FCSTD DOCUMENT  (FreeCAD 0.19R24276 (Git))
Label: Machine
License: All rights reserved
LicenseURL: http://en.wikipedia.org/wiki/All_rights_reserved
objects: Part::Feature×122, TechDraw::DrawViewDimension×35, Sketcher::SketchObject×31, PartDesign::Hole×19, PartDesign::Body×13, App::DocumentObjectGroup×9, App::Part×8, PartDesign::FeatureBase×7, PartDesign::Pad×6, PartDesign::Pocket×4, PartDesign::SubShapeBinder×3, TechDraw::DrawSVGTemplate×2, TechDraw::DrawViewPart×2, TechDraw::DrawViewAnnotation×2, TechDraw::DrawPage×2, Spreadsheet::Sheet×1, Mesh::Feature×1, App::VRMLObject×1, App::Link×1
note: 234 computed .brp shape members not serialized (recipe doc carries the construction recipe); baked Part::Feature solids carry a one-line shape summary decoded from their .brp

FEATURE [Sketcher::SketchObject] Sketch003
  FullyConstrained = false
  MapMode = 5
  Placement = pos=(0,0,0) rot=(1,0,0;1.5708rad)
  Support = -> [XZ_Plane002]
  expr: Constraints[11] = Spreadsheet.machine_heigh
  expr: Constraints[34] = 25 + Spreadsheet.rail_wheel_outer_clearing
  expr: Constraints[35] = 25 + Spreadsheet.rail_wheel_outer_clearing
  sketch-geometry (15):
    g0: LineSegment StartX=-20 StartY=140 StartZ=0 EndX=26 EndY=140 EndZ=0
    g1: LineSegment StartX=26 StartY=140 StartZ=0 EndX=26 EndY=0 EndZ=0
    g2: LineSegment StartX=26 StartY=0 StartZ=0 EndX=-20 EndY=0 EndZ=0
    g3: LineSegment StartX=-20 StartY=0 StartZ=0 EndX=-20 EndY=140 EndZ=0
    g4: GeomPoint X=0 Y=0 Z=0
    g5: LineSegment StartX=3.41 StartY=104.4 StartZ=0 EndX=11.59 EndY=104.4 EndZ=0
    g6: LineSegment StartX=13.5 StartY=102.49 StartZ=0 EndX=13.5 EndY=101.04 EndZ=0
    g7: LineSegment StartX=11.59 StartY=99.13 StartZ=0 EndX=3.41 EndY=99.13 EndZ=0
    g8: LineSegment StartX=1.5 StartY=101.04 StartZ=0 EndX=1.5 EndY=102.49 EndZ=0
    g9: ArcOfCircle CenterX=3.41 CenterY=102.49 CenterZ=0 NormalX=0 NormalY=0 NormalZ=1 AngleXU=0 Radius=1.91 StartAngle=1.5708 EndAngle=3.14159
    g10: ArcOfCircle CenterX=3.41 CenterY=101.04 CenterZ=0 NormalX=0 NormalY=0 NormalZ=1 AngleXU=0 Radius=1.91 StartAngle=3.14159 EndAngle=4.71239
    g11: ArcOfCircle CenterX=11.59 CenterY=102.49 CenterZ=0 NormalX=0 NormalY=0 NormalZ=1 AngleXU=0 Radius=1.91 StartAngle=1e-16 EndAngle=1.5708
    g12: ArcOfCircle CenterX=11.59 CenterY=101.04 CenterZ=0 NormalX=0 NormalY=0 NormalZ=1 AngleXU=0 Radius=1.91 StartAngle=4.71239 EndAngle=6.28319
    g13: GeomPoint X=7.5 Y=99.13 Z=0
    g14: Circle CenterX=7.5 CenterY=120 CenterZ=0 NormalX=0 NormalY=0 NormalZ=1 AngleXU=0 Radius=4.20728
  constraints (36):
    c: Coincident(g0,g1)
    c: Coincident(g1,g2)
    c: Coincident(g2,g3)
    c: Coincident(g3,g0)
    c: Horizontal(g0)
    c: Horizontal(g2)
    c: Vertical(g1)
    c: Vertical(g3)
    c: DistanceX(g2,g2) = 46
    c: Horizontal(g4,g-1)
    c: Vertical(g4,g-1)
    c: DistanceY(g1,g1) = 140
    c: Horizontal(g5)
    c: Horizontal(g7)
    c: Vertical(g6)
    c: Vertical(g8)
    c: Tangent(g5,g9) = 1.5708
    c: Tangent(g8,g9) = 1.5708
    c: Tangent(g7,g10) = 1.5708
    c: Tangent(g8,g10) = 1.5708
    c: Tangent(g5,g11) = 1.5708
    c: Tangent(g6,g11) = 1.5708
    c: Tangent(g6,g12) = 1.5708
    c: Tangent(g7,g12) = 1.5708
    c: DistanceX(g8,g6) = 12
    c: Symmetric(g7,g7,g13)
    c: Equal(g12,g11)
    c: Equal(g11,g9)
    c: Equal(g9,g10)
    c: DistanceY(g14,g0) = 20
    c: DistanceY(g5,g14) = 15.6
    c: DistanceY(g7,g5) = 5.27
    c: DistanceY(g8,g8) = 1.45
    c: Block(g3)
    c: DistanceX(g0,g14) = 27.5
    c: DistanceX(g0,g13) = 27.5
FEATURE [PartDesign::Pad] Pad001  label="Frame Plate Body"
  Direction = (1,1,1)
  Length = 8
  Length2 = 100
  Placement = pos=(0,0,0) rot=(1,0,0;1.5708rad)
  Profile = -> Sketch003
  Reversed = true
  Type = 0
FEATURE [Sketcher::SketchObject] Sketch004
  ExternalGeometry = -> [Pad001,Sketch003]
  FullyConstrained = true
  MapMode = 5
  Placement = pos=(0,0,0) rot=(1,0,0;1.5708rad)
  Support = -> [XZ_Plane002]
  expr: Constraints[19] = Spreadsheet.machine_heigh - Spreadsheet.board_heigh_from_top - 35.1
  expr: Constraints[22] = Spreadsheet.machine_heigh - Spreadsheet.bed_support_height + 20
  expr: Constraints[26] = 25 + Spreadsheet.rail_wheel_outer_clearing
  sketch-geometry (10):
    g0: Circle CenterX=-10 CenterY=10 CenterZ=0 NormalX=0 NormalY=0 NormalZ=1 AngleXU=0 Radius=2.5
    g1: Circle CenterX=10 CenterY=10 CenterZ=0 NormalX=0 NormalY=0 NormalZ=1 AngleXU=0 Radius=2.5
    g2: LineSegment StartX=-10 StartY=10 StartZ=0 EndX=10 EndY=10 EndZ=0
    g3: GeomPoint X=0 Y=10 Z=0
    g4: Circle CenterX=7.5 CenterY=130 CenterZ=0 NormalX=0 NormalY=0 NormalZ=1 AngleXU=0 Radius=2.5
    g5: Circle CenterX=7.5 CenterY=110 CenterZ=0 NormalX=0 NormalY=0 NormalZ=1 AngleXU=0 Radius=2.5
    g6: Circle CenterX=-10 CenterY=44.9 CenterZ=0 NormalX=0 NormalY=0 NormalZ=1 AngleXU=0 Radius=2.5
    g7: Circle CenterX=10 CenterY=44.9 CenterZ=0 NormalX=0 NormalY=0 NormalZ=1 AngleXU=0 Radius=2.5
    g8: Circle CenterX=-10 CenterY=60.9 CenterZ=0 NormalX=0 NormalY=0 NormalZ=1 AngleXU=0 Radius=2.5
    g9: Circle CenterX=10 CenterY=60.9 CenterZ=0 NormalX=0 NormalY=0 NormalZ=1 AngleXU=0 Radius=2.5
  constraints (27):
    c: Radius(g0) = 2.5
    c: Equal(g0,g1)
    c: Horizontal(g0,g1)
    c: DistanceX(g0,g1) = 20
    c: Coincident(g2,g0)
    c: Coincident(g2,g1)
    c: Symmetric(g2,g2,g3)
    c: Vertical(g3,g-1)
    c: DistanceY(g-1,g3) = 10
    c: Vertical(g5,g4)
    c: Equal(g5,g4)
    c: Equal(g4,g1)
    c: DistanceY(g5,g4) = 20
    c: DistanceY(g4,g-5) = 10
    c: Equal(g6,g7)
    c: Equal(g7,g0)
    c: Vertical(g6,g0)
    c: Vertical(g7,g1)
    c: Horizontal(g6,g7)
    c: DistanceY(g-4,g6) = 44.9
    c: Equal(g8,g9)
    c: Equal(g9,g6)
    c: DistanceY(g-1,g8) = 60.9
    c: Horizontal(g8,g9)
    c: Vertical(g6,g8)
    c: Vertical(g7,g9)
    c: DistanceX(g-3,g4) = 27.5
FEATURE [PartDesign::Hole] Hole  label="Frame Plate Mount Holes 1"
  BaseFeature = -> Pad001
  Depth = 25
  DepthType = 0
  Diameter = 5.5
  DrillForDepth = false
  DrillPoint = 0
  DrillPointAngle = 118
  HoleCutCountersinkAngle = 90
  HoleCutCustomValues = false
  HoleCutDepth = 5.4
  HoleCutDiameter = 9.2
  HoleCutType = 0
  ModelActualThread = false
  Placement = pos=(0,0,0) rot=(1,0,0;1.5708rad)
  Profile = -> Sketch004
  Tapered = false
  TaperedAngle = 90
  ThreadAngle = 0
  ThreadClass = 0
  ThreadCutOffInner = 0
  ThreadCutOffOuter = 0
  ThreadDirection = 0
  ThreadFit = 0
  ThreadPitch = 0
  ThreadSize = 13
  ThreadType = 1
  Threaded = false
FEATURE [PartDesign::Body] Body002  label="Front Left Plate Frame"
  Group = -> [Sketch003,Pad001,Sketch004,Hole]
  Origin = -> Origin002
  Placement = pos=(20,0,0) rot=(0,0,1;3.14159rad)
  Tip = -> Hole
  expr: .Placement.Base.x = 20
FEATURE [Part::Feature] Part__Feature001  label="Y-Axis Left Rail"
  Placement = pos=(12.5,0,120) rot=(-1,0,0;1.5708rad)
  shape: bbox 20 x 500 x 40 mm, 116 faces (baked)
  expr: .Placement.Base.z = Spreadsheet.machine_heigh - 20
  expr: .Placement.Base.x = 10 + Spreadsheet.rail_wheel_outer_clearing
FEATURE [PartDesign::FeatureBase] Clone
  BaseFeature = -> Body002
  Placement = pos=(0,0,0) rot=(0,0,1;3.14159rad)
FEATURE [PartDesign::Body] Body  label="Back Left Plate Frame"
  BaseFeature = -> Body002
  Group = -> [Clone]
  Origin = -> Origin
  Placement = pos=(20,508,0) rot=(0,0,1;0rad)
  Tip = -> Clone
  expr: .Placement.Base.x = 20
FEATURE [PartDesign::FeatureBase] Clone001
  BaseFeature = -> Body002
  Placement = pos=(0,0,0) rot=(0,0,1;3.14159rad)
FEATURE [PartDesign::Body] Body003  label="Front Right Plate Frame"
  BaseFeature = -> Body002
  Group = -> [Clone001]
  Origin = -> Origin003
  Placement = pos=(980,-8,0) rot=(0,0,1;3.14159rad)
  Tip = -> Clone001
  expr: .Placement.Base.x = Spreadsheet.machine_length - 20
FEATURE [PartDesign::FeatureBase] Clone002
  BaseFeature = -> Body002
  Placement = pos=(0,0,0) rot=(0,0,1;3.14159rad)
FEATURE [PartDesign::Body] Body004  label="Back Right Plate Frame"
  BaseFeature = -> Body002
  Group = -> [Clone002]
  Origin = -> Origin004
  Placement = pos=(980,500,0) rot=(0,0,1;3.14159rad)
  Tip = -> Clone002
  expr: .Placement.Base.x = Spreadsheet.machine_length - 20
FEATURE [Part::Feature] Part__Feature007  label="Y-Axis Right Rail"
  Placement = pos=(987.5,0,120) rot=(-1,0,0;1.5708rad)
  shape: bbox 20 x 500 x 40 mm, 116 faces (baked)
  expr: .Placement.Base.z = Spreadsheet.machine_heigh - 20
  expr: .Placement.Base.x = Spreadsheet.machine_length - 10 - Spreadsheet.rail_wheel_outer_clearing
FEATURE [Sketcher::SketchObject] Sketch005
  FullyConstrained = true
  MapMode = 5
  Support = -> [XY_Plane005]
  expr: Constraints[9] = Spreadsheet.machine_width
  expr: Constraints[10] = Spreadsheet.machine_length
  sketch-geometry (4):
    g0: LineSegment StartX=0 StartY=500 StartZ=0 EndX=1000 EndY=500 EndZ=0
    g1: LineSegment StartX=1000 StartY=500 StartZ=0 EndX=1000 EndY=180 EndZ=0
    g2: LineSegment StartX=1000 StartY=180 StartZ=0 EndX=0 EndY=180 EndZ=0
    g3: LineSegment StartX=0 StartY=180 StartZ=0 EndX=0 EndY=500 EndZ=0
  constraints (12):
    c: Coincident(g0,g1)
    c: Coincident(g1,g2)
    c: Coincident(g2,g3)
    c: Coincident(g3,g0)
    c: Horizontal(g0)
    c: Horizontal(g2)
    c: Vertical(g1)
    c: Vertical(g3)
    c: Vertical(g2,g-1)
    c: DistanceY(g-1,g0) = 500
    c: DistanceX(g0,g0) = 1000
    c: DistanceY(g3,g3) = 320
FEATURE [PartDesign::Pad] Pad
  Direction = (1,1,1)
  Length = 20
  Length2 = 100
  Profile = -> Sketch005
  Type = 0
  expr: Length = Spreadsheet.bed_thickness
FEATURE [PartDesign::Body] Body005  label="Bed"
  Group = -> [Sketch005,Pad]
  Origin = -> Origin005
  Placement = pos=(0,0,50.9) rot=(0,0,1;0rad)
  Tip = -> Pad
  expr: .Placement.Base.z = Spreadsheet.machine_heigh - Spreadsheet.bed_support_height + 10
FEATURE [Part::Feature] Part__Feature008  label="Right001"
  shape: bbox 144 x 13.2 x 66.48 mm, 79 faces (baked)
FEATURE [Part::Feature] Part__Feature009  label="Left001"
  shape: bbox 144 x 15 x 195 mm, 149 faces (baked)
FEATURE [App::Part] Boolean
  Group = -> [Part__Feature008,Part__Feature009]
  Origin = -> Origin006
  Placement = pos=(570,80,80) rot=(0,0,-1;1.5708rad)
  expr: .Placement.Base.x = Spreadsheet.machine_length / 2 + 70
  expr: .Placement.Base.z = Spreadsheet.machine_heigh - Spreadsheet.board_heigh_from_top
FEATURE [Spreadsheet::Sheet] Spreadsheet
  cells = A2=Bed Thickness; B2(bed_thickness)=20; E2=Bed Support Height; F2(bed_support_height)==board_heigh_from_top + bed_thickness + board_fix_heigh + 10; A3=Board Heigh; B3(board_heigh)=80; A4=Board Fix Height; B4(board_fix_heigh)=9.1; A5=Rail Wheel Width; B5(rail_wheel_width)=11; A6=Rail Wheel Spacers; B6(rail_wheel_spacers)=7; A7=Rail Wheel Outer Clearing; B7(rail_wheel_outer_clearing)=2.5; A8=Machine Width; B8(machine_width)=500; A9=Machine Length; B9(machine_length)=1000; A10=Power Supply Length; B10(power_supply_length)=210; A11=Machine Heigh; B11(machine_heigh)=140; A12=Board Heigh From Top; B12(board_heigh_from_top)=60; A13=Y Axis Position; B13(y_axis_pos)=283; D13=75; E13=475
FEATURE [Mesh::Feature] ed1_board_support  label="ed1-board-support"
  Placement = pos=(430,190,75.45) rot=(0,0,1;0rad)
  expr: .Placement.Base.x = Spreadsheet.machine_length / 2 - 70
  expr: .Placement.Base.z = -Spreadsheet.board_fix_heigh / 2 + Spreadsheet.machine_heigh - Spreadsheet.board_heigh_from_top
FEATURE [Sketcher::SketchObject] Sketch009
  FullyConstrained = true
  expr: Constraints[11] = Spreadsheet.machine_width
  expr: Constraints[10] = Spreadsheet.machine_length
  sketch-geometry (4):
    g0: LineSegment StartX=0 StartY=500 StartZ=0 EndX=1000 EndY=500 EndZ=0
    g1: LineSegment StartX=1000 StartY=500 StartZ=0 EndX=1000 EndY=0 EndZ=0
    g2: LineSegment StartX=1000 StartY=0 StartZ=0 EndX=0 EndY=0 EndZ=0
    g3: LineSegment StartX=0 StartY=0 StartZ=0 EndX=0 EndY=500 EndZ=0
  constraints (12):
    c: Coincident(g0,g1)
    c: Coincident(g1,g2)
    c: Coincident(g2,g3)
    c: Coincident(g3,g0)
    c: Horizontal(g0)
    c: Horizontal(g2)
    c: Vertical(g1)
    c: Vertical(g3)
    c: Vertical(g2,g-1)
    c: Horizontal(g2,g-1)
    c: DistanceX(g0,g0) = 1000
    c: DistanceY(g3,g3) = 500
FEATURE [App::DocumentObjectGroup] Group004  label="Feeder"
  Group = -> [Boolean]
FEATURE [Part::Feature] Part__Feature106  label="Bottom Camera"
  Placement = pos=(500,102.5,40.9) rot=(1,0,0;1.5708rad)
  shape: bbox 38.04 x 38.04 x 27.94 mm, 666 faces, 0 solids (baked)
  expr: .Placement.Base.z = Spreadsheet.board_heigh - Spreadsheet.board_fix_heigh - 30
  expr: .Placement.Base.x = Spreadsheet.machine_length / 2
FEATURE [Part::Feature] Part__Feature107  label="V-Slot 20x40x1000 Linear Rail"
  Placement = pos=(0,306.5,165) rot=(0.57735,0.57735,0.57735;2.0944rad)
  shape: bbox 1000 x 20 x 40 mm, 116 faces (baked)
  expr: .Placement.Base.y = Spreadsheet.y_axis_pos + 23.5
  expr: .Placement.Base.z = Spreadsheet.machine_heigh + 25
  expr: .Placement.Base.x = 0
FEATURE [App::VRMLObject] OpenPNPControl
  Placement = pos=(955,508,25) rot=(0,0,-1;1.5708rad)
FEATURE [Part::Feature] Part__Feature120  label="Bottom Right Frame"
  Placement = pos=(980,0,10) rot=(0.57735,-0.57735,-0.57735;4.18879rad)
  shape: bbox 40 x 500 x 20 mm, 116 faces (baked)
  expr: .Placement.Base.x = Spreadsheet.machine_length - 20
  expr: .Placement.Base.z = 10
FEATURE [Part::Feature] Part__Feature121  label="Bottom Left Frame"
  Placement = pos=(20,0,10) rot=(0.57735,-0.57735,-0.57735;4.18879rad)
  shape: bbox 40 x 500 x 20 mm, 116 faces (baked)
  expr: .Placement.Base.x = 20
FEATURE [Part::Feature] Part__Feature014  label="SWP (Basis)"
  Placement = pos=(-2.4e-14,1.75,57) rot=(-1,0,0;1.5708rad)
  shape: bbox 215 x 51.27 x 114 mm, 686 faces (baked)
FEATURE [Part::Feature] Part__Feature015  label="SWP (Deksel)"
  Placement = pos=(-18.25,51.25,57) rot=(-1,0,0;1.5708rad)
  shape: bbox 195 x 25.77 x 110.5 mm, 202 faces (baked)
FEATURE [Part::Feature] Part__Feature016  label="Slotted Countersunk Flat Head Screw_DIN_ISO 2009 - M3 x 5 --- 5N"
  Placement = pos=(-154,44.75,114) rot=(0.706406,-0.044508,-0.706406;3.23055rad)
  shape: bbox 5.5 x 5.5 x 5 mm, 14 faces (baked)
FEATURE [Part::Feature] Part__Feature017  label="Slotted Countersunk Flat Head Screw_DIN_ISO 2009 - M3 x 5 --- 5N001"
  Placement = pos=(-33,44.75,114) rot=(-0.51498,0.685268,0.51498;1.94005rad)
  shape: bbox 5.5 x 5.5 x 5 mm, 14 faces (baked)
FEATURE [Part::Feature] Part__Feature018  label="Slotted Countersunk Flat Head Screw_DIN_ISO 2009 - M3 x 5 --- 5N002"
  Placement = pos=(-154,44.75,6.765e-12) rot=(0.57735,0.57735,0.57735;4.18879rad)
  shape: bbox 5.5 x 5.5 x 5 mm, 14 faces (baked)
FEATURE [Part::Feature] Part__Feature019  label="Slotted Countersunk Flat Head Screw_DIN_ISO 2009 - M3 x 5 --- 5N003"
  Placement = pos=(-33,44.75,6.772e-12) rot=(0.24005,-0.940613,0.24005;1.63198rad)
  shape: bbox 5.5 x 5.5 x 5 mm, 14 faces (baked)
FEATURE [Part::Feature] Part__Feature020  label="Slotted Countersunk Flat Head Screw_DIN_ISO 2009 - M3 x 5 --- 5N004"
  Placement = pos=(-215,44.75,102) rot=(-1,0,0;2.08794rad)
  shape: bbox 5 x 5.5 x 5.5 mm, 14 faces (baked)
FEATURE [Part::Feature] Part__Feature021  label="Slotted Countersunk Flat Head Screw_DIN_ISO 2009 - M3 x 5 --- 5N005"
  Placement = pos=(-215,44.75,12) rot=(-1,0,0;0.866489rad)
  shape: bbox 5 x 5.5 x 5.5 mm, 14 faces (baked)
FEATURE [Part::Feature] Part__Feature022  label="Body 60mm fan"
  Placement = pos=(-170.75,34.3,77.75) rot=(-1,0,0;1.5708rad)
  shape: bbox 59.5 x 15.2 x 59.5 mm, 105 faces (baked)
FEATURE [Part::Feature] Part__Feature023  label="Propellor 60mm fan"
  Placement = pos=(-170.75,44.3,77.75) rot=(-0.793222,0.430581,0.430581;1.8004rad)
  shape: bbox 57.7 x 10.4 x 57.19 mm, 97 faces (baked)
FEATURE [Part::Feature] Part__Feature024  label="Slotted Countersunk Flat Head Screw_DIN_ISO 2009 - M3 x 20 --- 20N"
  Placement = pos=(-145.75,51.25,52.75) rot=(0.700883,-0.700883,0.13239;3.40484rad)
  shape: bbox 5.5 x 20 x 5.5 mm, 14 faces (baked)
FEATURE [Part::Feature] Part__Feature025  label="Slotted Countersunk Flat Head Screw_DIN_ISO 2009 - M3 x 20 --- 20N001"
  Placement = pos=(-195.75,51.25,102.75) rot=(0.672053,-0.672053,0.310951;3.74454rad)
  shape: bbox 5.5 x 20 x 5.5 mm, 14 faces (baked)
FEATURE [Part::Feature] Part__Feature026  label="SWP (M3 moer)"
  Placement = pos=(-205,-1.3e-14,104.5) rot=(-1,0,0;1.5708rad)
  shape: bbox 8.083 x 3.75 x 7 mm, 29 faces (baked)
FEATURE [Part::Feature] Part__Feature027  label="SWP (M3 moer)001"
  Placement = pos=(-205,0,9.5) rot=(-1,0,0;1.5708rad)
  shape: bbox 8.083 x 3.75 x 7 mm, 29 faces (baked)
FEATURE [Part::Feature] Part__Feature028  label="SWP (M3 moer)002"
  Placement = pos=(-117.5,-7e-15,50.05) rot=(-1,0,0;1.5708rad)
  shape: bbox 8.083 x 3.75 x 7 mm, 29 faces (baked)
FEATURE [Part::Feature] Part__Feature029  label="SWP (M3 moer)003"
  Placement = pos=(-27.5,-1.3e-14,104.5) rot=(-1,0,0;1.5708rad)
  shape: bbox 8.083 x 3.75 x 7 mm, 29 faces (baked)
FEATURE [Part::Feature] Part__Feature030  label="SWP (M3 moer)004"
  Placement = pos=(-27.5,-1e-15,9.5) rot=(-1,0,0;1.5708rad)
  shape: bbox 8.083 x 3.75 x 7 mm, 29 faces (baked)
FEATURE [Part::Feature] Part__Feature031  label="SWP (PCB)"
  Placement = pos=(-1.75,9.75,57) rot=(-1,0,0;1.5708rad)
  shape: bbox 211.5 x 15.9 x 110.5 mm, 247 faces (baked)
FEATURE [Part::Feature] Part__Feature032  label="SWP (Montage draad)"
  Placement = pos=(-9.8,18.4,88.95) rot=(0.57735,0.57735,0.57735;4.18879rad)
  shape: bbox 9.9 x 4.25 x 7 mm, 32 faces (baked)
FEATURE [Part::Feature] Part__Feature033  label="SWP (Montage draad 2)"
  Placement = pos=(-9.8,18.4,88.95) rot=(-1,0,0;1.5708rad)
  shape: bbox 7 x 1 x 7 mm, 27 faces (baked)
FEATURE [Part::Feature] Part__Feature034  label="Slotted Cheese Head Screw_DIN_ISO 1207 - M4 x 5 --- 5N"
  Placement = pos=(-9.8,22,88.95) rot=(-0.497229,0.497229,-0.711004;1.90545rad)
  shape: bbox 7.022 x 7.6 x 7 mm, 13 faces (baked)
FEATURE [Part::Feature] Part__Feature035  label="SWP (Montage draad)001"
  Placement = pos=(-9.8,18.4,79.45) rot=(0.57735,0.57735,0.57735;4.18879rad)
  shape: bbox 9.9 x 4.25 x 7 mm, 32 faces (baked)
FEATURE [Part::Feature] Part__Feature036  label="SWP (Montage draad)002"
  Placement = pos=(-9.8,18.4,69.95) rot=(0.57735,0.57735,0.57735;4.18879rad)
  shape: bbox 9.9 x 4.25 x 7 mm, 32 faces (baked)
FEATURE [Part::Feature] Part__Feature037  label="SWP (Montage draad)003"
  Placement = pos=(-9.8,18.4,60.45) rot=(0.57735,0.57735,0.57735;4.18879rad)
  shape: bbox 9.9 x 4.25 x 7 mm, 32 faces (baked)
FEATURE [Part::Feature] Part__Feature038  label="SWP (Montage draad)004"
  Placement = pos=(-9.8,18.4,50.95) rot=(0.57735,0.57735,0.57735;4.18879rad)
  shape: bbox 9.9 x 4.25 x 7 mm, 32 faces (baked)
FEATURE [Part::Feature] Part__Feature039  label="SWP (Montage draad)005"
  Placement = pos=(-9.8,18.4,41.45) rot=(0.57735,0.57735,0.57735;4.18879rad)
  shape: bbox 9.9 x 4.25 x 7 mm, 32 faces (baked)
FEATURE [Part::Feature] Part__Feature040  label="SWP (Montage draad)006"
  Placement = pos=(-9.8,18.4,31.95) rot=(0.57735,0.57735,0.57735;4.18879rad)
  shape: bbox 9.9 x 4.25 x 7 mm, 32 faces (baked)
FEATURE [Part::Feature] Part__Feature041  label="SWP (Montage draad)007"
  Placement = pos=(-9.8,18.4,22.45) rot=(0.57735,0.57735,0.57735;4.18879rad)
  shape: bbox 9.9 x 4.25 x 7 mm, 32 faces (baked)
FEATURE [Part::Feature] Part__Feature042  label="SWP (Montage draad)008"
  Placement = pos=(-9.8,18.4,12.95) rot=(0.57735,0.57735,0.57735;4.18879rad)
  shape: bbox 9.9 x 4.25 x 7 mm, 32 faces (baked)
FEATURE [Part::Feature] Part__Feature043  label="SWP (Montage draad 2)001"
  Placement = pos=(-9.8,18.4,79.45) rot=(-1,0,0;1.5708rad)
  shape: bbox 7 x 1 x 7 mm, 27 faces (baked)
FEATURE [Part::Feature] Part__Feature044  label="SWP (Montage draad 2)002"
  Placement = pos=(-9.8,18.4,69.95) rot=(-1,0,0;1.5708rad)
  shape: bbox 7 x 1 x 7 mm, 27 faces (baked)
FEATURE [Part::Feature] Part__Feature045  label="SWP (Montage draad 2)003"
  Placement = pos=(-9.8,18.4,60.45) rot=(-1,0,0;1.5708rad)
  shape: bbox 7 x 1 x 7 mm, 27 faces (baked)
FEATURE [Part::Feature] Part__Feature046  label="SWP (Montage draad 2)004"
  Placement = pos=(-9.8,18.4,50.95) rot=(-1,0,0;1.5708rad)
  shape: bbox 7 x 1 x 7 mm, 27 faces (baked)
FEATURE [Part::Feature] Part__Feature047  label="SWP (Montage draad 2)005"
  Placement = pos=(-9.8,18.4,41.45) rot=(-1,0,0;1.5708rad)
  shape: bbox 7 x 1 x 7 mm, 27 faces (baked)
FEATURE [Part::Feature] Part__Feature048  label="SWP (Montage draad 2)006"
  Placement = pos=(-9.8,18.4,31.95) rot=(-1,0,0;1.5708rad)
  shape: bbox 7 x 1 x 7 mm, 27 faces (baked)
FEATURE [Part::Feature] Part__Feature049  label="SWP (Montage draad 2)007"
  Placement = pos=(-9.8,18.4,22.45) rot=(-1,0,0;1.5708rad)
  shape: bbox 7 x 1 x 7 mm, 27 faces (baked)
FEATURE [Part::Feature] Part__Feature050  label="SWP (Montage draad 2)008"
  Placement = pos=(-9.8,18.4,12.95) rot=(-1,0,0;1.5708rad)
  shape: bbox 7 x 1 x 7 mm, 27 faces (baked)
FEATURE [Part::Feature] Part__Feature051  label="Slotted Cheese Head Screw_DIN_ISO 1207 - M4 x 5 --- 5N001"
  Placement = pos=(-9.8,22,79.45) rot=(-0.497229,0.497229,-0.711004;1.90545rad)
  shape: bbox 7.022 x 7.6 x 7 mm, 13 faces (baked)
FEATURE [Part::Feature] Part__Feature052  label="Slotted Cheese Head Screw_DIN_ISO 1207 - M4 x 5 --- 5N002"
  Placement = pos=(-9.8,22,69.95) rot=(-0.497229,0.497229,-0.711004;1.90545rad)
  shape: bbox 7.022 x 7.6 x 7 mm, 13 faces (baked)
FEATURE [Part::Feature] Part__Feature053  label="Slotted Cheese Head Screw_DIN_ISO 1207 - M4 x 5 --- 5N003"
  Placement = pos=(-9.8,22,60.45) rot=(-0.497229,0.497229,-0.711004;1.90545rad)
  shape: bbox 7.022 x 7.6 x 7 mm, 13 faces (baked)
FEATURE [Part::Feature] Part__Feature054  label="Slotted Cheese Head Screw_DIN_ISO 1207 - M4 x 5 --- 5N004"
  Placement = pos=(-9.8,22,50.95) rot=(-0.497229,0.497229,-0.711004;1.90545rad)
  shape: bbox 7.022 x 7.6 x 7 mm, 13 faces (baked)
FEATURE [Part::Feature] Part__Feature055  label="Slotted Cheese Head Screw_DIN_ISO 1207 - M4 x 5 --- 5N005"
  Placement = pos=(-9.8,22,41.45) rot=(-0.497229,0.497229,-0.711004;1.90545rad)
  shape: bbox 7.022 x 7.6 x 7 mm, 13 faces (baked)
FEATURE [Part::Feature] Part__Feature056  label="Slotted Cheese Head Screw_DIN_ISO 1207 - M4 x 5 --- 5N006"
  Placement = pos=(-9.8,22,31.95) rot=(-0.497229,0.497229,-0.711004;1.90545rad)
  shape: bbox 7.022 x 7.6 x 7 mm, 13 faces (baked)
FEATURE [Part::Feature] Part__Feature057  label="Slotted Cheese Head Screw_DIN_ISO 1207 - M4 x 5 --- 5N007"
  Placement = pos=(-9.8,22,22.45) rot=(-0.497229,0.497229,-0.711004;1.90545rad)
  shape: bbox 7.022 x 7.6 x 7 mm, 13 faces (baked)
FEATURE [Part::Feature] Part__Feature058  label="Slotted Cheese Head Screw_DIN_ISO 1207 - M4 x 5 --- 5N008"
  Placement = pos=(-9.8,22,12.95) rot=(-0.497229,0.497229,-0.711004;1.90545rad)
  shape: bbox 7.022 x 7.6 x 7 mm, 13 faces (baked)
FEATURE [Part::Feature] Part__Feature059  label="SWP (switch)"
  Placement = pos=(-128.5,14.3,-4.2e-14) rot=(0,1,0;3.14159rad)
  shape: bbox 19 x 12.1 x 6 mm, 97 faces (baked)
FEATURE [App::Part] Switching_power_supply  label="24 V power supply"
  Group = -> [Part__Feature014,Part__Feature015,Part__Feature016,Part__Feature017,Part__Feature018,Part__Feature019,Part__Feature020,Part__Feature021,Part__Feature022,Part__Feature023,Part__Feature024,Part__Feature025,Part__Feature026,Part__Feature027,Part__Feature028,Part__Feature029,Part__Feature030,Part__Feature031,Part__Feature032,Part__Feature033,Part__Feature034,Part__Feature035,Part__Feature036,+23 more]
  Origin = -> Origin009
  Placement = pos=(576,346,20) rot=(0,0.707107,0.707107;3.14159rad)
FEATURE [Part::Feature] Part__Feature060  label="SWP (Basis)001"
  Placement = pos=(-2.4e-14,1.75,57) rot=(-1,0,0;1.5708rad)
  shape: bbox 215 x 51.27 x 114 mm, 686 faces (baked)
FEATURE [Part::Feature] Part__Feature061  label="SWP (Deksel)001"
  Placement = pos=(-18.25,51.25,57) rot=(-1,0,0;1.5708rad)
  shape: bbox 195 x 25.77 x 110.5 mm, 202 faces (baked)
FEATURE [Part::Feature] Part__Feature062  label="Slotted Countersunk Flat Head Screw_DIN_ISO 2009 - M3 x 5 --- 5N006"
  Placement = pos=(-154,44.75,114) rot=(0.706406,-0.044508,-0.706406;3.23055rad)
  shape: bbox 5.5 x 5.5 x 5 mm, 14 faces (baked)
FEATURE [Part::Feature] Part__Feature063  label="Slotted Countersunk Flat Head Screw_DIN_ISO 2009 - M3 x 5 --- 5N007"
  Placement = pos=(-33,44.75,114) rot=(-0.51498,0.685268,0.51498;1.94005rad)
  shape: bbox 5.5 x 5.5 x 5 mm, 14 faces (baked)
FEATURE [Part::Feature] Part__Feature064  label="Slotted Countersunk Flat Head Screw_DIN_ISO 2009 - M3 x 5 --- 5N008"
  Placement = pos=(-154,44.75,6.765e-12) rot=(0.57735,0.57735,0.57735;4.18879rad)
  shape: bbox 5.5 x 5.5 x 5 mm, 14 faces (baked)
FEATURE [Part::Feature] Part__Feature065  label="Slotted Countersunk Flat Head Screw_DIN_ISO 2009 - M3 x 5 --- 5N009"
  Placement = pos=(-33,44.75,6.772e-12) rot=(0.24005,-0.940613,0.24005;1.63198rad)
  shape: bbox 5.5 x 5.5 x 5 mm, 14 faces (baked)
FEATURE [Part::Feature] Part__Feature066  label="Slotted Countersunk Flat Head Screw_DIN_ISO 2009 - M3 x 5 --- 5N010"
  Placement = pos=(-215,44.75,102) rot=(-1,0,0;2.08794rad)
  shape: bbox 5 x 5.5 x 5.5 mm, 14 faces (baked)
FEATURE [Part::Feature] Part__Feature067  label="Slotted Countersunk Flat Head Screw_DIN_ISO 2009 - M3 x 5 --- 5N011"
  Placement = pos=(-215,44.75,12) rot=(-1,0,0;0.866489rad)
  shape: bbox 5 x 5.5 x 5.5 mm, 14 faces (baked)
FEATURE [Part::Feature] Part__Feature068  label="Body 60mm fan001"
  Placement = pos=(-170.75,34.3,77.75) rot=(-1,0,0;1.5708rad)
  shape: bbox 59.5 x 15.2 x 59.5 mm, 105 faces (baked)
FEATURE [Part::Feature] Part__Feature069  label="Propellor 60mm fan001"
  Placement = pos=(-170.75,44.3,77.75) rot=(-0.793222,0.430581,0.430581;1.8004rad)
  shape: bbox 57.7 x 10.4 x 57.19 mm, 97 faces (baked)
FEATURE [Part::Feature] Part__Feature070  label="Slotted Countersunk Flat Head Screw_DIN_ISO 2009 - M3 x 20 --- 20N002"
  Placement = pos=(-145.75,51.25,52.75) rot=(0.700883,-0.700883,0.13239;3.40484rad)
  shape: bbox 5.5 x 20 x 5.5 mm, 14 faces (baked)
FEATURE [Part::Feature] Part__Feature071  label="Slotted Countersunk Flat Head Screw_DIN_ISO 2009 - M3 x 20 --- 20N003"
  Placement = pos=(-195.75,51.25,102.75) rot=(0.672053,-0.672053,0.310951;3.74454rad)
  shape: bbox 5.5 x 20 x 5.5 mm, 14 faces (baked)
FEATURE [Part::Feature] Part__Feature072  label="SWP (M3 moer)005"
  Placement = pos=(-205,-1.3e-14,104.5) rot=(-1,0,0;1.5708rad)
  shape: bbox 8.083 x 3.75 x 7 mm, 29 faces (baked)
FEATURE [Part::Feature] Part__Feature073  label="SWP (M3 moer)006"
  Placement = pos=(-205,0,9.5) rot=(-1,0,0;1.5708rad)
  shape: bbox 8.083 x 3.75 x 7 mm, 29 faces (baked)
FEATURE [Part::Feature] Part__Feature074  label="SWP (M3 moer)007"
  Placement = pos=(-117.5,-7e-15,50.05) rot=(-1,0,0;1.5708rad)
  shape: bbox 8.083 x 3.75 x 7 mm, 29 faces (baked)
FEATURE [Part::Feature] Part__Feature075  label="SWP (M3 moer)008"
  Placement = pos=(-27.5,-1.3e-14,104.5) rot=(-1,0,0;1.5708rad)
  shape: bbox 8.083 x 3.75 x 7 mm, 29 faces (baked)
FEATURE [Part::Feature] Part__Feature076  label="SWP (M3 moer)009"
  Placement = pos=(-27.5,-1e-15,9.5) rot=(-1,0,0;1.5708rad)
  shape: bbox 8.083 x 3.75 x 7 mm, 29 faces (baked)
FEATURE [Part::Feature] Part__Feature077  label="SWP (PCB)001"
  Placement = pos=(-1.75,9.75,57) rot=(-1,0,0;1.5708rad)
  shape: bbox 211.5 x 15.9 x 110.5 mm, 247 faces (baked)
FEATURE [Part::Feature] Part__Feature078  label="SWP (Montage draad)009"
  Placement = pos=(-9.8,18.4,88.95) rot=(0.57735,0.57735,0.57735;4.18879rad)
  shape: bbox 9.9 x 4.25 x 7 mm, 32 faces (baked)
FEATURE [Part::Feature] Part__Feature079  label="SWP (Montage draad 2)009"
  Placement = pos=(-9.8,18.4,88.95) rot=(-1,0,0;1.5708rad)
  shape: bbox 7 x 1 x 7 mm, 27 faces (baked)
FEATURE [Part::Feature] Part__Feature080  label="Slotted Cheese Head Screw_DIN_ISO 1207 - M4 x 5 --- 5N009"
  Placement = pos=(-9.8,22,88.95) rot=(-0.497229,0.497229,-0.711004;1.90545rad)
  shape: bbox 7.022 x 7.6 x 7 mm, 13 faces (baked)
FEATURE [Part::Feature] Part__Feature081  label="SWP (Montage draad)010"
  Placement = pos=(-9.8,18.4,79.45) rot=(0.57735,0.57735,0.57735;4.18879rad)
  shape: bbox 9.9 x 4.25 x 7 mm, 32 faces (baked)
FEATURE [Part::Feature] Part__Feature082  label="SWP (Montage draad)011"
  Placement = pos=(-9.8,18.4,69.95) rot=(0.57735,0.57735,0.57735;4.18879rad)
  shape: bbox 9.9 x 4.25 x 7 mm, 32 faces (baked)
FEATURE [Part::Feature] Part__Feature083  label="SWP (Montage draad)012"
  Placement = pos=(-9.8,18.4,60.45) rot=(0.57735,0.57735,0.57735;4.18879rad)
  shape: bbox 9.9 x 4.25 x 7 mm, 32 faces (baked)
FEATURE [Part::Feature] Part__Feature084  label="SWP (Montage draad)013"
  Placement = pos=(-9.8,18.4,50.95) rot=(0.57735,0.57735,0.57735;4.18879rad)
  shape: bbox 9.9 x 4.25 x 7 mm, 32 faces (baked)
FEATURE [Part::Feature] Part__Feature085  label="SWP (Montage draad)014"
  Placement = pos=(-9.8,18.4,41.45) rot=(0.57735,0.57735,0.57735;4.18879rad)
  shape: bbox 9.9 x 4.25 x 7 mm, 32 faces (baked)
FEATURE [Part::Feature] Part__Feature086  label="SWP (Montage draad)015"
  Placement = pos=(-9.8,18.4,31.95) rot=(0.57735,0.57735,0.57735;4.18879rad)
  shape: bbox 9.9 x 4.25 x 7 mm, 32 faces (baked)
FEATURE [Part::Feature] Part__Feature087  label="SWP (Montage draad)016"
  Placement = pos=(-9.8,18.4,22.45) rot=(0.57735,0.57735,0.57735;4.18879rad)
  shape: bbox 9.9 x 4.25 x 7 mm, 32 faces (baked)
FEATURE [Part::Feature] Part__Feature088  label="SWP (Montage draad)017"
  Placement = pos=(-9.8,18.4,12.95) rot=(0.57735,0.57735,0.57735;4.18879rad)
  shape: bbox 9.9 x 4.25 x 7 mm, 32 faces (baked)
FEATURE [Part::Feature] Part__Feature089  label="SWP (Montage draad 2)010"
  Placement = pos=(-9.8,18.4,79.45) rot=(-1,0,0;1.5708rad)
  shape: bbox 7 x 1 x 7 mm, 27 faces (baked)
FEATURE [Part::Feature] Part__Feature090  label="SWP (Montage draad 2)011"
  Placement = pos=(-9.8,18.4,69.95) rot=(-1,0,0;1.5708rad)
  shape: bbox 7 x 1 x 7 mm, 27 faces (baked)
FEATURE [Part::Feature] Part__Feature091  label="SWP (Montage draad 2)012"
  Placement = pos=(-9.8,18.4,60.45) rot=(-1,0,0;1.5708rad)
  shape: bbox 7 x 1 x 7 mm, 27 faces (baked)
FEATURE [Part::Feature] Part__Feature092  label="SWP (Montage draad 2)013"
  Placement = pos=(-9.8,18.4,50.95) rot=(-1,0,0;1.5708rad)
  shape: bbox 7 x 1 x 7 mm, 27 faces (baked)
FEATURE [Part::Feature] Part__Feature093  label="SWP (Montage draad 2)014"
  Placement = pos=(-9.8,18.4,41.45) rot=(-1,0,0;1.5708rad)
  shape: bbox 7 x 1 x 7 mm, 27 faces (baked)
FEATURE [Part::Feature] Part__Feature094  label="SWP (Montage draad 2)015"
  Placement = pos=(-9.8,18.4,31.95) rot=(-1,0,0;1.5708rad)
  shape: bbox 7 x 1 x 7 mm, 27 faces (baked)
FEATURE [Part::Feature] Part__Feature095  label="SWP (Montage draad 2)016"
  Placement = pos=(-9.8,18.4,22.45) rot=(-1,0,0;1.5708rad)
  shape: bbox 7 x 1 x 7 mm, 27 faces (baked)
FEATURE [Part::Feature] Part__Feature096  label="SWP (Montage draad 2)017"
  Placement = pos=(-9.8,18.4,12.95) rot=(-1,0,0;1.5708rad)
  shape: bbox 7 x 1 x 7 mm, 27 faces (baked)
FEATURE [Part::Feature] Part__Feature097  label="Slotted Cheese Head Screw_DIN_ISO 1207 - M4 x 5 --- 5N010"
  Placement = pos=(-9.8,22,79.45) rot=(-0.497229,0.497229,-0.711004;1.90545rad)
  shape: bbox 7.022 x 7.6 x 7 mm, 13 faces (baked)
FEATURE [Part::Feature] Part__Feature098  label="Slotted Cheese Head Screw_DIN_ISO 1207 - M4 x 5 --- 5N011"
  Placement = pos=(-9.8,22,69.95) rot=(-0.497229,0.497229,-0.711004;1.90545rad)
  shape: bbox 7.022 x 7.6 x 7 mm, 13 faces (baked)
FEATURE [Part::Feature] Part__Feature099  label="Slotted Cheese Head Screw_DIN_ISO 1207 - M4 x 5 --- 5N012"
  Placement = pos=(-9.8,22,60.45) rot=(-0.497229,0.497229,-0.711004;1.90545rad)
  shape: bbox 7.022 x 7.6 x 7 mm, 13 faces (baked)
FEATURE [Part::Feature] Part__Feature100  label="Slotted Cheese Head Screw_DIN_ISO 1207 - M4 x 5 --- 5N013"
  Placement = pos=(-9.8,22,50.95) rot=(-0.497229,0.497229,-0.711004;1.90545rad)
  shape: bbox 7.022 x 7.6 x 7 mm, 13 faces (baked)
FEATURE [Part::Feature] Part__Feature101  label="Slotted Cheese Head Screw_DIN_ISO 1207 - M4 x 5 --- 5N014"
  Placement = pos=(-9.8,22,41.45) rot=(-0.497229,0.497229,-0.711004;1.90545rad)
  shape: bbox 7.022 x 7.6 x 7 mm, 13 faces (baked)
FEATURE [Part::Feature] Part__Feature102  label="Slotted Cheese Head Screw_DIN_ISO 1207 - M4 x 5 --- 5N015"
  Placement = pos=(-9.8,22,31.95) rot=(-0.497229,0.497229,-0.711004;1.90545rad)
  shape: bbox 7.022 x 7.6 x 7 mm, 13 faces (baked)
FEATURE [Part::Feature] Part__Feature103  label="Slotted Cheese Head Screw_DIN_ISO 1207 - M4 x 5 --- 5N016"
  Placement = pos=(-9.8,22,22.45) rot=(-0.497229,0.497229,-0.711004;1.90545rad)
  shape: bbox 7.022 x 7.6 x 7 mm, 13 faces (baked)
FEATURE [Part::Feature] Part__Feature104  label="Slotted Cheese Head Screw_DIN_ISO 1207 - M4 x 5 --- 5N017"
  Placement = pos=(-9.8,22,12.95) rot=(-0.497229,0.497229,-0.711004;1.90545rad)
  shape: bbox 7.022 x 7.6 x 7 mm, 13 faces (baked)
FEATURE [Part::Feature] Part__Feature105  label="SWP (switch)001"
  Placement = pos=(-128.5,14.3,-4.2e-14) rot=(0,1,0;3.14159rad)
  shape: bbox 19 x 12.1 x 6 mm, 97 faces (baked)
FEATURE [App::Part] Switching_power_supply001  label="12 V power supply"
  Group = -> [Part__Feature060,Part__Feature061,Part__Feature062,Part__Feature063,Part__Feature064,Part__Feature065,Part__Feature066,Part__Feature067,Part__Feature068,Part__Feature069,Part__Feature070,Part__Feature071,Part__Feature072,Part__Feature073,Part__Feature074,Part__Feature075,Part__Feature076,Part__Feature077,Part__Feature078,Part__Feature079,Part__Feature080,Part__Feature081,Part__Feature082,+23 more]
  Origin = -> Origin010
  Placement = pos=(576,222,20) rot=(0,0.707107,0.707107;3.14159rad)
FEATURE [App::DocumentObjectGroup] Group005  label="Electronics"
  Group = -> [Switching_power_supply001,Switching_power_supply,Part__Feature106,OpenPNPControl]
FEATURE [Part::Feature] Feeder_8mm_Frame_fix001001001
  Placement = pos=(572.59,75,78.99) rot=(0,0,-1;1.5708rad)
  shape: bbox 84.4 x 9.9 x 20 mm, 453 faces, 0 solids (baked)
  expr: .Placement.Base.x = -69.45 + 84.40000000000001 + Spreadsheet.machine_length / 2 + 70 - 6.16 - 6.2
  expr: .Placement.Base.z = 44.74 - 20 + Spreadsheet.machine_heigh - Spreadsheet.board_heigh_from_top - 25.1 - 0.65
FEATURE [Part::Feature] Part__Feature123  label="Feeder Support Back"
  Placement = pos=(0,70,44.9) rot=(0,1,0;1.5708rad)
  shape: bbox 1000 x 20 x 20 mm, 72 faces (baked)
  expr: .Placement.Base.z = Spreadsheet.machine_heigh - Spreadsheet.board_heigh_from_top - 35.1
FEATURE [Part::Feature] Part__Feature124  label="Feeder Support Front"
  Placement = pos=(0,10,44.9) rot=(0,1,0;1.5708rad)
  shape: bbox 1000 x 20 x 20 mm, 72 faces (baked)
  expr: .Placement.Base.z = Spreadsheet.machine_heigh - Spreadsheet.board_heigh_from_top - 35.1
FEATURE [App::DocumentObjectGroup] Group003  label="Crossbar"
  Group = -> [Part__Feature123,Part__Feature124]
FEATURE [Sketcher::SketchObject] Sketch015
  FullyConstrained = true
  MapMode = 5
  Placement = pos=(0,0,0) rot=(0.57735,0.57735,0.57735;2.0944rad)
  Support = -> [YZ_Plane013]
  expr: Constraints[20] = Spreadsheet.machine_heigh - Spreadsheet.bed_support_height + 30
  expr: Constraints[7] = Spreadsheet.machine_width
  sketch-geometry (7):
    g0: LineSegment StartX=500 StartY=70.9 StartZ=0 EndX=500 EndY=0 EndZ=0
    g1: LineSegment StartX=500 StartY=0 StartZ=0 EndX=0 EndY=0 EndZ=0
    g2: LineSegment StartX=0 StartY=0 StartZ=0 EndX=0 EndY=54.9 EndZ=0
    g3: LineSegment StartX=0 StartY=54.9 StartZ=0 EndX=175 EndY=54.9 EndZ=0
    g4: LineSegment StartX=180 StartY=59.9 StartZ=0 EndX=180 EndY=70.9 EndZ=0
    g5: LineSegment StartX=180 StartY=70.9 StartZ=0 EndX=500 EndY=70.9 EndZ=0
    g6: ArcOfCircle CenterX=175 CenterY=59.9 CenterZ=0 NormalX=0 NormalY=0 NormalZ=1 AngleXU=0 Radius=5 StartAngle=4.71239 EndAngle=6.28319
  constraints (24):
    c: Coincident(g0,g1)
    c: Coincident(g1,g2)
    c: Horizontal(g1)
    c: Vertical(g0)
    c: Vertical(g2)
    c: Horizontal(g1,g-1)
    c: Vertical(g1,g-1)
    c: DistanceX(g1,g1) = 500
    c: Horizontal(g3)
    c: Vertical(g3,g2)
    c: Block(g2)
    c: Horizontal(g3,g2)
    c: Vertical(g4)
    c: Horizontal(g5)
    c: Horizontal(g5,g4)
    c: Vertical(g5,g4)
    c: Vertical(g0,g5)
    c: DistanceX(g5,g5) = 320
    c: Block(g5)
    c: Horizontal(g0,g5)
    c: DistanceY(g0,g0) = 70.9
    c: Tangent(g3,g6) = -1.5708
    c: Tangent(g4,g6) = -1.5708
    c: Radius(g6) = 5
FEATURE [PartDesign::Pad] Pad004
  Direction = (1,1,1)
  Length = 6
  Length2 = 100
  Placement = pos=(0,0,0) rot=(0.57735,0.57735,0.57735;2.0944rad)
  Profile = -> Sketch015
  Reversed = true
  Type = 0
FEATURE [Sketcher::SketchObject] Sketch016
  ExternalGeometry = -> [Sketch015]
  FullyConstrained = false
  MapMode = 5
  Placement = pos=(0,0,0) rot=(0.57735,0.57735,0.57735;2.0944rad)
  Support = -> [YZ_Plane013]
  expr: Constraints[13] = Spreadsheet.machine_heigh - Spreadsheet.bed_support_height + 20
  expr: Constraints[10] = Spreadsheet.machine_heigh - Spreadsheet.board_heigh_from_top - 35.1
  sketch-geometry (42):
    g0: Circle CenterX=10 CenterY=44.9 CenterZ=0 NormalX=0 NormalY=0 NormalZ=1 AngleXU=0 Radius=2.5
    g1: Circle CenterX=10 CenterY=10 CenterZ=0 NormalX=0 NormalY=0 NormalZ=1 AngleXU=0 Radius=2.5
    g2: Circle CenterX=70 CenterY=44.9 CenterZ=0 NormalX=0 NormalY=0 NormalZ=1 AngleXU=0 Radius=2.5
    g3: Circle CenterX=70 CenterY=10 CenterZ=0 NormalX=0 NormalY=0 NormalZ=1 AngleXU=0 Radius=2.5
    g4: Circle CenterX=190 CenterY=60.9 CenterZ=0 NormalX=0 NormalY=0 NormalZ=1 AngleXU=0 Radius=2.5
    g5: Circle CenterX=210 CenterY=60.9 CenterZ=0 NormalX=0 NormalY=0 NormalZ=1 AngleXU=0 Radius=2.5
    g6: Circle CenterX=230 CenterY=60.9 CenterZ=0 NormalX=0 NormalY=0 NormalZ=1 AngleXU=0 Radius=2.5
    g7: LineSegment StartX=210 StartY=60.9 StartZ=0 EndX=230 EndY=60.9 EndZ=0
    g8: Circle CenterX=250 CenterY=60.9 CenterZ=0 NormalX=0 NormalY=0 NormalZ=1 AngleXU=0 Radius=2.5
    g9: LineSegment StartX=230 StartY=60.9 StartZ=0 EndX=250 EndY=60.9 EndZ=0
    g10: Circle CenterX=270 CenterY=60.9 CenterZ=0 NormalX=0 NormalY=0 NormalZ=1 AngleXU=0 Radius=2.5
    g11: LineSegment StartX=250 StartY=60.9 StartZ=0 EndX=270 EndY=60.9 EndZ=0
    g12: Circle CenterX=290 CenterY=60.9 CenterZ=0 NormalX=0 NormalY=0 NormalZ=1 AngleXU=0 Radius=2.5
    g13: LineSegment StartX=270 StartY=60.9 StartZ=0 EndX=290 EndY=60.9 EndZ=0
    g14: Circle CenterX=310 CenterY=60.9 CenterZ=0 NormalX=0 NormalY=0 NormalZ=1 AngleXU=0 Radius=2.5
    g15: LineSegment StartX=290 StartY=60.9 StartZ=0 EndX=310 EndY=60.9 EndZ=0
    g16: Circle CenterX=330 CenterY=60.9 CenterZ=0 NormalX=0 NormalY=0 NormalZ=1 AngleXU=0 Radius=2.5
    g17: LineSegment StartX=310 StartY=60.9 StartZ=0 EndX=330 EndY=60.9 EndZ=0
    g18: Circle CenterX=350 CenterY=60.9 CenterZ=0 NormalX=0 NormalY=0 NormalZ=1 AngleXU=0 Radius=2.5
    g19: LineSegment StartX=330 StartY=60.9 StartZ=0 EndX=350 EndY=60.9 EndZ=0
    g20: Circle CenterX=370 CenterY=60.9 CenterZ=0 NormalX=0 NormalY=0 NormalZ=1 AngleXU=0 Radius=2.5
    g21: LineSegment StartX=350 StartY=60.9 StartZ=0 EndX=370 EndY=60.9 EndZ=0
    g22: Circle CenterX=390 CenterY=60.9 CenterZ=0 NormalX=0 NormalY=0 NormalZ=1 AngleXU=0 Radius=2.5
    g23: LineSegment StartX=370 StartY=60.9 StartZ=0 EndX=390 EndY=60.9 EndZ=0
    g24: Circle CenterX=410 CenterY=60.9 CenterZ=0 NormalX=0 NormalY=0 NormalZ=1 AngleXU=0 Radius=2.5
    g25: LineSegment StartX=390 StartY=60.9 StartZ=0 EndX=410 EndY=60.9 EndZ=0
    g26: Circle CenterX=430 CenterY=60.9 CenterZ=0 NormalX=0 NormalY=0 NormalZ=1 AngleXU=0 Radius=2.5
    g27: LineSegment StartX=410 StartY=60.9 StartZ=0 EndX=430 EndY=60.9 EndZ=0
    g28: Circle CenterX=450 CenterY=60.9 CenterZ=0 NormalX=0 NormalY=0 NormalZ=1 AngleXU=0 Radius=2.5
    g29: LineSegment StartX=430 StartY=60.9 StartZ=0 EndX=450 EndY=60.9 EndZ=0
    g30: Circle CenterX=470 CenterY=60.9 CenterZ=0 NormalX=0 NormalY=0 NormalZ=1 AngleXU=0 Radius=2.5
    g31: LineSegment StartX=450 StartY=60.9 StartZ=0 EndX=470 EndY=60.9 EndZ=0
    g32: Circle CenterX=490 CenterY=60.9 CenterZ=0 NormalX=0 NormalY=0 NormalZ=1 AngleXU=0 Radius=2.5
    g33: LineSegment StartX=470 StartY=60.9 StartZ=0 EndX=490 EndY=60.9 EndZ=0
    g34: Circle CenterX=170 CenterY=10 CenterZ=0 NormalX=0 NormalY=0 NormalZ=1 AngleXU=0 Radius=2.5
    g35: Circle CenterX=250 CenterY=10 CenterZ=0 NormalX=0 NormalY=0 NormalZ=1 AngleXU=0 Radius=2.5
    g36: Circle CenterX=330 CenterY=10 CenterZ=0 NormalX=0 NormalY=0 NormalZ=1 AngleXU=0 Radius=2.5
    g37: Circle CenterX=410 CenterY=10 CenterZ=0 NormalX=0 NormalY=0 NormalZ=1 AngleXU=0 Radius=2.5
    g38: Circle CenterX=490 CenterY=10 CenterZ=0 NormalX=0 NormalY=0 NormalZ=1 AngleXU=0 Radius=2.5
    g39: Circle CenterX=120 CenterY=10 CenterZ=0 NormalX=0 NormalY=0 NormalZ=1 AngleXU=0 Radius=2.5
    g40: LineSegment StartX=70 StartY=10 StartZ=0 EndX=170 EndY=10 EndZ=0
    g41: GeomPoint X=120 Y=10 Z=0
  constraints (94):
    c: Radius(g0) = 2.5
    c: Equal(g0,g2)
    c: Equal(g2,g3)
    c: Equal(g3,g1)
    c: Horizontal(g0,g2)
    c: Horizontal(g1,g3)
    c: Vertical(g0,g1)
    c: DistanceX(g0,g2) = 60
    c: Vertical(g2,g3)
    c: DistanceX(g-1,g1) = 10
    c: DistanceY(g-1,g0) = 44.9
    c: DistanceY(g-1,g1) = 10
    c: Equal(g0,g4)
    c: DistanceY(g-1,g4) = 60.9
    c: DistanceX(g-3,g4) = 10
    c: Equal(g4,g5)
    c: Coincident(g5,g7)
    c: Coincident(g6,g7)
    c: Distance(g7) = 20
    c: Angle(g7) = 0
    c: Coincident(g6,g9)
    c: Coincident(g8,g9)
    c: Equal(g7,g9)
    c: Parallel(g9,g7)
    c: Coincident(g8,g11)
    c: Coincident(g10,g11)
    c: Equal(g7,g11)
    c: Parallel(g11,g7)
    c: Coincident(g10,g13)
    c: Coincident(g12,g13)
    c: Equal(g7,g13)
    c: Parallel(g13,g7)
    c: Coincident(g12,g15)
    c: Coincident(g14,g15)
    c: Equal(g7,g15)
    c: Parallel(g15,g7)
    c: Coincident(g14,g17)
    c: Coincident(g16,g17)
    c: Equal(g7,g17)
    c: Parallel(g17,g7)
    c: Coincident(g16,g19)
    c: Coincident(g18,g19)
    c: Equal(g7,g19)
    c: Parallel(g19,g7)
    c: Coincident(g18,g21)
    c: Coincident(g20,g21)
    c: Equal(g7,g21)
    c: Parallel(g21,g7)
    c: Coincident(g20,g23)
    c: Coincident(g22,g23)
    c: Equal(g7,g23)
    c: Parallel(g23,g7)
    c: Coincident(g22,g25)
    c: Coincident(g24,g25)
    c: Equal(g7,g25)
    c: Parallel(g25,g7)
    c: Coincident(g24,g27)
    c: Coincident(g26,g27)
    c: Equal(g7,g27)
    c: Parallel(g27,g7)
    c: Coincident(g26,g29)
    c: Coincident(g28,g29)
    c: Equal(g7,g29)
    c: Parallel(g29,g7)
    c: Coincident(g28,g31)
    c: Coincident(g30,g31)
    c: Equal(g7,g31)
    c: Parallel(g31,g7)
    c: Coincident(g30,g33)
    c: Coincident(g32,g33)
    c: Equal(g7,g33)
    c: Parallel(g33,g7)
    c: Horizontal(g5,g4)
    c: DistanceX(g4,g5) = 20
    c: Equal(g34,g35)
    c: Equal(g35,g36)
    c: Equal(g36,g37)
    c: Equal(g37,g38)
    c: Equal(g38,g4)
    c: Horizontal(g34,g35)
    c: Horizontal(g35,g36)
    c: Horizontal(g36,g37)
    c: Horizontal(g37,g38)
    c: Vertical(g38,g32)
    c: Vertical(g16,g36)
    c: Vertical(g8,g35)
    c: Vertical(g24,g37)
    c: DistanceY(g-1,g34) = 10
    c: Equal(g39,g4)
    c: DistanceX(g34,g35) = 80
    c: Coincident(g40,g3)
    c: Coincident(g40,g34)
    c: Symmetric(g40,g40,g41)
    c: Coincident(g39,g41)
FEATURE [PartDesign::Hole] Hole005
  BaseFeature = -> Pad004
  Depth = 25
  DepthType = 0
  Diameter = 5.5
  DrillForDepth = false
  DrillPoint = 1
  DrillPointAngle = 118
  HoleCutCountersinkAngle = 90
  HoleCutCustomValues = false
  HoleCutDepth = 0
  HoleCutDiameter = 6.1
  HoleCutType = 0
  ModelActualThread = false
  Placement = pos=(0,0,0) rot=(0.57735,0.57735,0.57735;2.0944rad)
  Profile = -> Sketch016
  Tapered = false
  TaperedAngle = 90
  ThreadAngle = 0
  ThreadClass = 0
  ThreadCutOffInner = 0
  ThreadCutOffOuter = 0
  ThreadDirection = 0
  ThreadFit = 0
  ThreadPitch = 0
  ThreadSize = 13
  ThreadType = 1
  Threaded = false
FEATURE [PartDesign::Body] Body009  label="Left Side Cover"
  Group = -> [Sketch015,Pad004,Sketch016,Hole005]
  Origin = -> Origin013
  Tip = -> Hole005
FEATURE [App::DocumentObjectGroup] Group001  label="Left"
  Group = -> [Part__Feature001,Part__Feature121,Body002,Body,Body009]
FEATURE [PartDesign::FeatureBase] Clone003
  BaseFeature = -> Body009
FEATURE [PartDesign::Body] Body010  label="Right Side Cover"
  BaseFeature = -> Body009
  Group = -> [Clone003]
  Origin = -> Origin014
  Placement = pos=(1006,0,0) rot=(0,0,1;0rad)
  Tip = -> Clone003
  expr: .Placement.Base.x = Spreadsheet.machine_length + 6
FEATURE [App::DocumentObjectGroup] Group002  label="Right"
  Group = -> [Part__Feature007,Body003,Body004,Part__Feature120,Body010]
FEATURE [App::DocumentObjectGroup] Group  label="Frame"
  Group = -> [Group001,Group002,Group003]
FEATURE [TechDraw::DrawSVGTemplate] Template
  EditableTexts = AUTHOR_NAME=<owner>.org; DN=DN; DRAWING_TITLE=Side Cover; FC-DATE=DD/MM/YYYY; FC-REV=REV A; FC-SC=SCALE; FC-SH=X / Y; FC-SI=A4; FreeCAD_DRAWING=Whitecat Desktop PNP; PN=WHC-DESK-PNP-SIDE-COV; SI-1=Material: 6061-T5 Aluminium 6mm
  Height = 210
  Orientation = 1
  Width = 297
FEATURE [TechDraw::DrawViewPart] View
  CoarseView = false
  Direction = (1,0,0)
  Focus = 100
  HardHidden = false
  IsoCount = 0
  IsoHidden = false
  IsoVisible = false
  LockPosition = false
  Perspective = false
  Rotation = 0
  Scale = 0.4
  ScaleType = 2
  SeamHidden = false
  SeamVisible = true
  SmoothHidden = false
  SmoothVisible = true
  Source = -> [Body009]
  X = 154.42
  XDirection = (0,1,0)
  Y = 96.2975
FEATURE [TechDraw::DrawViewDimension] Dimension
  Arbitrary = false
  ArbitraryTolerances = false
  EqualTolerance = true
  FormatSpec = %.2f
  FormatSpecOverTolerance = %+.2f
  FormatSpecUnderTolerance = %+.2f
  Inverted = false
  LockPosition = false
  MeasureType = 1
  OverTolerance = 0
  References2D = -> [View]
  Rotation = 0
  ScaleType = 0
  TheoreticalExact = false
  Type = 1
  UnderTolerance = 0
  X = -83.5017
  Y = 3.28167
FEATURE [TechDraw::DrawViewDimension] Dimension001
  Arbitrary = false
  ArbitraryTolerances = false
  EqualTolerance = true
  FormatSpec = %.2f
  FormatSpecOverTolerance = %+.2f
  FormatSpecUnderTolerance = %+.2f
  Inverted = false
  LockPosition = false
  MeasureType = 1
  OverTolerance = 0
  References2D = -> [View]
  Rotation = 0
  ScaleType = 0
  TheoreticalExact = false
  Type = 2
  UnderTolerance = 0
  X = -115.594
  Y = -19.3503
FEATURE [TechDraw::DrawViewDimension] Dimension002
  Arbitrary = false
  ArbitraryTolerances = false
  EqualTolerance = true
  FormatSpec = %.2f
  FormatSpecOverTolerance = %+.2f
  FormatSpecUnderTolerance = %+.2f
  Inverted = false
  LockPosition = false
  MeasureType = 1
  OverTolerance = 0
  References2D = -> [View]
  Rotation = 0
  ScaleType = 0
  TheoreticalExact = false
  Type = 2
  UnderTolerance = 0
  X = -122.603
  Y = -2.96531
FEATURE [TechDraw::DrawViewDimension] Dimension003
  Arbitrary = false
  ArbitraryTolerances = false
  EqualTolerance = true
  FormatSpec = %.2f
  FormatSpecOverTolerance = %+.2f
  FormatSpecUnderTolerance = %+.2f
  Inverted = false
  LockPosition = false
  MeasureType = 1
  OverTolerance = 0
  References2D = -> [View]
  Rotation = 0
  ScaleType = 0
  TheoreticalExact = false
  Type = 1
  UnderTolerance = 0
  X = -88.5318
  Y = -26.9637
FEATURE [TechDraw::DrawViewDimension] Dimension004
  Arbitrary = false
  ArbitraryTolerances = false
  EqualTolerance = true
  FormatSpec = %.2f
  FormatSpecOverTolerance = %+.2f
  FormatSpecUnderTolerance = %+.2f
  Inverted = false
  LockPosition = false
  MeasureType = 1
  OverTolerance = 0
  References2D = -> [View]
  Rotation = 0
  ScaleType = 0
  TheoreticalExact = false
  Type = 1
  UnderTolerance = 0
  X = -84
  Y = -20.3126
FEATURE [TechDraw::DrawViewDimension] Dimension005
  Arbitrary = false
  ArbitraryTolerances = false
  EqualTolerance = true
  FormatSpec = %.2f
  FormatSpecOverTolerance = %+.2f
  FormatSpecUnderTolerance = %+.2f
  Inverted = false
  LockPosition = false
  MeasureType = 1
  OverTolerance = 0
  References2D = -> [View]
  Rotation = 0
  ScaleType = 0
  TheoreticalExact = false
  Type = 1
  UnderTolerance = 0
  X = -61.5701
  Y = -20.3242
FEATURE [TechDraw::DrawViewDimension] Dimension006
  Arbitrary = false
  ArbitraryTolerances = false
  EqualTolerance = true
  FormatSpec = %.2f
  FormatSpecOverTolerance = %+.2f
  FormatSpecUnderTolerance = %+.2f
  Inverted = false
  LockPosition = false
  MeasureType = 1
  OverTolerance = 0
  References2D = -> [View]
  Rotation = 0
  ScaleType = 0
  TheoreticalExact = false
  Type = 1
  UnderTolerance = 0
  X = -41.8391
  Y = -20.3277
FEATURE [TechDraw::DrawViewDimension] Dimension007
  Arbitrary = false
  ArbitraryTolerances = false
  EqualTolerance = true
  FormatSpec = %.2f
  FormatSpecOverTolerance = %+.2f
  FormatSpecUnderTolerance = %+.2f
  Inverted = false
  LockPosition = false
  MeasureType = 1
  OverTolerance = 0
  References2D = -> [View]
  Rotation = 0
  ScaleType = 0
  TheoreticalExact = false
  Type = 2
  UnderTolerance = 0
  X = -65.9346
  Y = -2.66928
FEATURE [TechDraw::DrawViewDimension] Dimension008
  Arbitrary = false
  ArbitraryTolerances = false
  EqualTolerance = true
  FormatSpec = %.2f
  FormatSpecOverTolerance = %+.2f
  FormatSpecUnderTolerance = %+.2f
  Inverted = false
  LockPosition = false
  MeasureType = 1
  OverTolerance = 0
  References2D = -> [View]
  Rotation = 0
  ScaleType = 0
  TheoreticalExact = false
  Type = 1
  UnderTolerance = 0
  X = -16.139
  Y = -20.3264
FEATURE [TechDraw::DrawViewDimension] Dimension009
  Arbitrary = false
  ArbitraryTolerances = false
  EqualTolerance = true
  FormatSpec = %.2f
  FormatSpecOverTolerance = %+.2f
  FormatSpecUnderTolerance = %+.2f
  Inverted = false
  LockPosition = false
  MeasureType = 1
  OverTolerance = 0
  References2D = -> [View]
  Rotation = 0
  ScaleType = 0
  TheoreticalExact = false
  Type = 1
  UnderTolerance = 0
  X = 15.8147
  Y = -20.3399
FEATURE [TechDraw::DrawViewDimension] Dimension010
  Arbitrary = false
  ArbitraryTolerances = false
  EqualTolerance = true
  FormatSpec = %.2f
  FormatSpecOverTolerance = %+.2f
  FormatSpecUnderTolerance = %+.2f
  Inverted = false
  LockPosition = false
  MeasureType = 1
  OverTolerance = 0
  References2D = -> [View]
  Rotation = 0
  ScaleType = 0
  TheoreticalExact = false
  Type = 1
  UnderTolerance = 0
  X = 47.2294
  Y = -20.3574
FEATURE [TechDraw::DrawViewDimension] Dimension011
  Arbitrary = false
  ArbitraryTolerances = false
  EqualTolerance = true
  FormatSpec = %.2f
  FormatSpecOverTolerance = %+.2f
  FormatSpecUnderTolerance = %+.2f
  Inverted = false
  LockPosition = false
  MeasureType = 1
  OverTolerance = 0
  References2D = -> [View]
  Rotation = 0
  ScaleType = 0
  TheoreticalExact = false
  Type = 1
  UnderTolerance = 0
  X = 80.9493
  Y = -20.3125
FEATURE [TechDraw::DrawViewDimension] Dimension012
  Arbitrary = false
  ArbitraryTolerances = false
  EqualTolerance = true
  FormatSpec = %.2f
  FormatSpecOverTolerance = %+.2f
  FormatSpecUnderTolerance = %+.2f
  Inverted = false
  LockPosition = false
  MeasureType = 1
  OverTolerance = 0
  References2D = -> [View]
  Rotation = 0
  ScaleType = 0
  TheoreticalExact = false
  Type = 2
  UnderTolerance = 0
  X = 120.06
  Y = -0.589735
FEATURE [TechDraw::DrawViewDimension] Dimension014
  Arbitrary = false
  ArbitraryTolerances = false
  EqualTolerance = true
  FormatSpec = R%.2f
  FormatSpecOverTolerance = %+.2f
  FormatSpecUnderTolerance = %+.2f
  Inverted = false
  LockPosition = false
  MeasureType = 1
  OverTolerance = 0
  References2D = -> [View]
  Rotation = 0
  ScaleType = 0
  TheoreticalExact = false
  Type = 4
  UnderTolerance = 0
  X = -32.7318
  Y = 16.9581
FEATURE [TechDraw::DrawViewDimension] Dimension015
  Arbitrary = false
  ArbitraryTolerances = false
  EqualTolerance = true
  FormatSpec = %.2f
  FormatSpecOverTolerance = %+.2f
  FormatSpecUnderTolerance = %+.2f
  Inverted = false
  LockPosition = false
  MeasureType = 1
  OverTolerance = 0
  References2D = -> [View]
  Rotation = 0
  ScaleType = 0
  TheoreticalExact = false
  Type = 2
  UnderTolerance = 0
  X = 112.656
  Y = 22.3467
FEATURE [TechDraw::DrawViewDimension] Dimension016
  Arbitrary = false
  ArbitraryTolerances = false
  EqualTolerance = true
  FormatSpec = %.2f
  FormatSpecOverTolerance = %+.2f
  FormatSpecUnderTolerance = %+.2f
  Inverted = false
  LockPosition = false
  MeasureType = 1
  OverTolerance = 0
  References2D = -> [View]
  Rotation = 0
  ScaleType = 0
  TheoreticalExact = false
  Type = 1
  UnderTolerance = 0
  X = 106.114
  Y = 25.3312
FEATURE [TechDraw::DrawViewDimension] Dimension017
  Arbitrary = false
  ArbitraryTolerances = false
  EqualTolerance = true
  FormatSpec = %.2f
  FormatSpecOverTolerance = %+.2f
  FormatSpecUnderTolerance = %+.2f
  Inverted = false
  LockPosition = false
  MeasureType = 1
  OverTolerance = 0
  References2D = -> [View]
  Rotation = 0
  ScaleType = 0
  TheoreticalExact = false
  Type = 1
  UnderTolerance = 0
  X = 51.3488
  Y = 24.9713
FEATURE [TechDraw::DrawViewDimension] Dimension018
  Arbitrary = false
  ArbitraryTolerances = false
  EqualTolerance = true
  FormatSpec = %.2f
  FormatSpecOverTolerance = %+.2f
  FormatSpecUnderTolerance = %+.2f
  Inverted = false
  LockPosition = false
  MeasureType = 1
  OverTolerance = 0
  References2D = -> [View]
  Rotation = 0
  ScaleType = 0
  TheoreticalExact = false
  Type = 1
  UnderTolerance = 0
  X = 35.4642
  Y = 30.657
FEATURE [TechDraw::DrawViewAnnotation] Annotation
  Font = osifont
  LineSpace = 80
  LockPosition = false
  MaxWidth = -1
  Rotation = 0
  ScaleType = 0
  Text = All holes spaced 20mm
  TextSize = 2
  TextStyle = 0
  X = 179.534
  Y = 117.838
FEATURE [TechDraw::DrawViewDimension] Dimension019
  Arbitrary = false
  ArbitraryTolerances = false
  EqualTolerance = true
  FormatSpec = %.2f
  FormatSpecOverTolerance = %+.2f
  FormatSpecUnderTolerance = %+.2f
  Inverted = false
  LockPosition = false
  MeasureType = 1
  OverTolerance = 0
  References2D = -> [View]
  Rotation = 0
  ScaleType = 0
  TheoreticalExact = false
  Type = 1
  UnderTolerance = 0
  X = -65.929
  Y = 30.6734
FEATURE [TechDraw::DrawViewDimension] Dimension020
  Arbitrary = false
  ArbitraryTolerances = false
  EqualTolerance = true
  FormatSpec = %.2f
  FormatSpecOverTolerance = %+.2f
  FormatSpecUnderTolerance = %+.2f
  Inverted = false
  LockPosition = false
  MeasureType = 1
  OverTolerance = 0
  References2D = -> [View]
  Rotation = 0
  ScaleType = 0
  TheoreticalExact = false
  Type = 2
  UnderTolerance = 0
  X = -110.051
  Y = 21.2329
FEATURE [TechDraw::DrawViewAnnotation] Annotation001
  Font = osifont
  LineSpace = 80
  LockPosition = false
  MaxWidth = -1
  Rotation = 0
  ScaleType = 0
  Text = All holes are non-threaded trough M5 holes
  TextSize = 5
  TextStyle = 0
  X = 63.7636
  Y = 177.903
FEATURE [TechDraw::DrawViewDimension] Dimension021
  Arbitrary = false
  ArbitraryTolerances = false
  EqualTolerance = true
  FormatSpec = %.2f
  FormatSpecOverTolerance = %+.2f
  FormatSpecUnderTolerance = %+.2f
  Inverted = false
  LockPosition = false
  MeasureType = 1
  OverTolerance = 0
  References2D = -> [View]
  Rotation = 0
  ScaleType = 0
  TheoreticalExact = false
  Type = 1
  UnderTolerance = 0
  X = -1.58485
  Y = 37.7463
FEATURE [TechDraw::DrawPage] Page  label="Side Cover"
  KeepUpdated = true
  NextBalloonIndex = 1
  ProjectionType = 0
  Template = -> Template
  Views = -> [View,Dimension,Dimension001,Dimension002,Dimension003,Dimension004,Dimension005,Dimension006,Dimension007,Dimension008,Dimension009,Dimension010,Dimension011,Dimension012,Dimension014,Dimension015,Dimension016,Dimension017,Dimension018,Annotation,Dimension019,Dimension020,Annotation001,Dimension021]
FEATURE [TechDraw::DrawSVGTemplate] Template001
  EditableTexts = AUTHOR_NAME=<owner>.org; DN=DN; DRAWING_TITLE=Frame Plate; FC-DATE=DD/MM/YYYY; FC-REV=REV A; FC-SC=SCALE; FC-SH=X / Y; FC-SI=A4; FreeCAD_DRAWING=Whitecat Desktop PNP; PN=WHC-DESK-PNP-FRM-PLT; SI-1=Material: 6061-T5 Aluminium 6mm
  Height = 210
  Orientation = 1
  Width = 297
FEATURE [TechDraw::DrawViewPart] View001
  CoarseView = false
  Direction = (0,1,0)
  Focus = 100
  HardHidden = false
  IsoCount = 0
  IsoHidden = false
  IsoVisible = false
  LockPosition = false
  Perspective = false
  Rotation = 0
  Scale = 0.75
  ScaleType = 0
  SeamHidden = false
  SeamVisible = true
  SmoothHidden = false
  SmoothVisible = true
  Source = -> [Body002]
  X = 148.5
  XDirection = (-1,0,0)
  Y = 124
FEATURE [TechDraw::DrawViewDimension] Dimension022
  Arbitrary = false
  ArbitraryTolerances = false
  EqualTolerance = true
  FormatSpec = %.2f
  FormatSpecOverTolerance = %+.2f
  FormatSpecUnderTolerance = %+.2f
  Inverted = false
  LockPosition = false
  MeasureType = 1
  OverTolerance = 0
  References2D = -> [View001]
  Rotation = 0
  ScaleType = 0
  TheoreticalExact = false
  Type = 1
  UnderTolerance = 0
  X = -0.571115
  Y = 62.4374
FEATURE [TechDraw::DrawViewDimension] Dimension023
  Arbitrary = false
  ArbitraryTolerances = false
  EqualTolerance = true
  FormatSpec = %.2f
  FormatSpecOverTolerance = %+.2f
  FormatSpecUnderTolerance = %+.2f
  Inverted = false
  LockPosition = false
  MeasureType = 1
  OverTolerance = 0
  References2D = -> [View001]
  Rotation = 0
  ScaleType = 0
  TheoreticalExact = false
  Type = 2
  UnderTolerance = 0
  X = -45.1779
  Y = -2.02703
FEATURE [TechDraw::DrawViewDimension] Dimension024
  Arbitrary = false
  ArbitraryTolerances = false
  EqualTolerance = true
  FormatSpec = %.2f
  FormatSpecOverTolerance = %+.2f
  FormatSpecUnderTolerance = %+.2f
  Inverted = false
  LockPosition = false
  MeasureType = 1
  OverTolerance = 0
  References2D = -> [View001]
  Rotation = 0
  ScaleType = 0
  TheoreticalExact = false
  Type = 2
  UnderTolerance = 0
  X = -24.0077
  Y = -58.5057
FEATURE [TechDraw::DrawViewDimension] Dimension025
  Arbitrary = false
  ArbitraryTolerances = false
  EqualTolerance = true
  FormatSpec = %.2f
  FormatSpecOverTolerance = %+.2f
  FormatSpecUnderTolerance = %+.2f
  Inverted = false
  LockPosition = false
  MeasureType = 1
  OverTolerance = 0
  References2D = -> [View001]
  Rotation = 0
  ScaleType = 0
  TheoreticalExact = false
  Type = 2
  UnderTolerance = 0
  X = -27.2007
  Y = -32.3091
FEATURE [TechDraw::DrawViewDimension] Dimension026
  Arbitrary = false
  ArbitraryTolerances = false
  EqualTolerance = true
  FormatSpec = %.2f
  FormatSpecOverTolerance = %+.2f
  FormatSpecUnderTolerance = %+.2f
  Inverted = false
  LockPosition = false
  MeasureType = 1
  OverTolerance = 0
  References2D = -> [View001]
  Rotation = 0
  ScaleType = 0
  TheoreticalExact = false
  Type = 2
  UnderTolerance = 0
  X = -32.9516
  Y = -32.6548
FEATURE [TechDraw::DrawViewDimension] Dimension027
  Arbitrary = false
  ArbitraryTolerances = false
  EqualTolerance = true
  FormatSpec = %.2f
  FormatSpecOverTolerance = %+.2f
  FormatSpecUnderTolerance = %+.2f
  Inverted = false
  LockPosition = false
  MeasureType = 1
  OverTolerance = 0
  References2D = -> [View001]
  Rotation = 0
  ScaleType = 0
  TheoreticalExact = false
  Type = 1
  UnderTolerance = 0
  X = -2.51793
  Y = -63.7735
FEATURE [TechDraw::DrawViewDimension] Dimension028
  Arbitrary = false
  ArbitraryTolerances = false
  EqualTolerance = true
  FormatSpec = %.2f
  FormatSpecOverTolerance = %+.2f
  FormatSpecUnderTolerance = %+.2f
  Inverted = false
  LockPosition = false
  MeasureType = 1
  OverTolerance = 0
  References2D = -> [View001]
  Rotation = 0
  ScaleType = 0
  TheoreticalExact = false
  Type = 1
  UnderTolerance = 0
  X = -1.75424
  Y = -35.4814
FEATURE [TechDraw::DrawViewDimension] Dimension029
  Arbitrary = false
  ArbitraryTolerances = false
  EqualTolerance = true
  FormatSpec = ⌀%.2f
  FormatSpecOverTolerance = %+.2f
  FormatSpecUnderTolerance = %+.2f
  Inverted = false
  LockPosition = false
  MeasureType = 1
  OverTolerance = 0
  References2D = -> [View001]
  Rotation = 0
  ScaleType = 0
  TheoreticalExact = false
  Type = 5
  UnderTolerance = 0
  X = 0.576483
  Y = 2.97456
FEATURE [TechDraw::DrawViewDimension] Dimension030
  Arbitrary = false
  ArbitraryTolerances = false
  EqualTolerance = true
  FormatSpec = %.2f
  FormatSpecOverTolerance = %+.2f
  FormatSpecUnderTolerance = %+.2f
  Inverted = false
  LockPosition = false
  MeasureType = 1
  OverTolerance = 0
  References2D = -> [View001]
  Rotation = 0
  ScaleType = 0
  TheoreticalExact = false
  Type = 2
  UnderTolerance = 0
  X = 21.8396
  Y = 20.0644
FEATURE [TechDraw::DrawViewDimension] Dimension031
  Arbitrary = false
  ArbitraryTolerances = false
  EqualTolerance = true
  FormatSpec = %.2f
  FormatSpecOverTolerance = %+.2f
  FormatSpecUnderTolerance = %+.2f
  Inverted = false
  LockPosition = false
  MeasureType = 1
  OverTolerance = 0
  References2D = -> [View001]
  Rotation = 0
  ScaleType = 0
  TheoreticalExact = false
  Type = 2
  UnderTolerance = 0
  X = 31.072
  Y = 41.4672
FEATURE [TechDraw::DrawViewDimension] Dimension032
  Arbitrary = false
  ArbitraryTolerances = false
  EqualTolerance = true
  FormatSpec = %.2f
  FormatSpecOverTolerance = %+.2f
  FormatSpecUnderTolerance = %+.2f
  Inverted = false
  LockPosition = false
  MeasureType = 1
  OverTolerance = 0
  References2D = -> [View001]
  Rotation = 0
  ScaleType = 0
  TheoreticalExact = false
  Type = 2
  UnderTolerance = 0
  X = -23.8815
  Y = 33.7611
FEATURE [TechDraw::DrawViewDimension] Dimension033
  Arbitrary = false
  ArbitraryTolerances = false
  EqualTolerance = true
  FormatSpec = %.2f
  FormatSpecOverTolerance = %+.2f
  FormatSpecUnderTolerance = %+.2f
  Inverted = false
  LockPosition = false
  MeasureType = 1
  OverTolerance = 0
  References2D = -> [View001]
  Rotation = 0
  ScaleType = 0
  TheoreticalExact = false
  Type = 1
  UnderTolerance = 0
  X = 3.0881
  Y = 18.3091
FEATURE [TechDraw::DrawViewDimension] Dimension034
  Arbitrary = false
  ArbitraryTolerances = false
  EqualTolerance = true
  FormatSpec = %.2f
  FormatSpecOverTolerance = %+.2f
  FormatSpecUnderTolerance = %+.2f
  Inverted = false
  LockPosition = false
  MeasureType = 1
  OverTolerance = 0
  References2D = -> [View001]
  Rotation = 0
  ScaleType = 0
  TheoreticalExact = false
  Type = 2
  UnderTolerance = 0
  X = -13.5934
  Y = 14.311
FEATURE [TechDraw::DrawViewDimension] Dimension035
  Arbitrary = false
  ArbitraryTolerances = false
  EqualTolerance = true
  FormatSpec = ⌀%.2f
  FormatSpecOverTolerance = %+.2f
  FormatSpecUnderTolerance = %+.2f
  Inverted = false
  LockPosition = false
  MeasureType = 1
  OverTolerance = 0
  References2D = -> [View001]
  Rotation = 0
  ScaleType = 0
  TheoreticalExact = false
  Type = 5
  UnderTolerance = 0
  X = -5.86524
  Y = 44.4238
FEATURE [TechDraw::DrawPage] Page001  label="Frame Plate"
  KeepUpdated = true
  NextBalloonIndex = 1
  ProjectionType = 0
  Template = -> Template001
  Views = -> [View001,Dimension022,Dimension023,Dimension024,Dimension025,Dimension026,Dimension027,Dimension028,Dimension029,Dimension030,Dimension031,Dimension032,Dimension033,Dimension034,Dimension035]
FEATURE [App::DocumentObjectGroup] Group008  label="Drawings"
  Group = -> [Page,Page001]
FEATURE [Sketcher::SketchObject] Sketch  label="y-plate-body"
  FullyConstrained = false
  MapMode = 5
  Support = -> [XY_Plane016]
  sketch-geometry (13):
    g0: LineSegment StartX=-53.5834 StartY=-36.7445 StartZ=0 EndX=-53.5834 EndY=3.25546 EndZ=0
    g1: LineSegment StartX=-53.5834 StartY=3.25546 StartZ=0 EndX=-13.5834 EndY=3.25546 EndZ=0
    g2: LineSegment StartX=-10.5834 StartY=6.25546 StartZ=0 EndX=-10.5834 EndY=27.0662 EndZ=0
    g3: LineSegment StartX=-7.5834 StartY=30.0662 StartZ=0 EndX=70.0566 EndY=30.0662 EndZ=0
    g4: LineSegment StartX=70.0566 StartY=30.0662 StartZ=0 EndX=70.0566 EndY=-97.5802 EndZ=0
    g5: LineSegment StartX=67.0566 StartY=-100.58 StartZ=0 EndX=-7.5834 EndY=-100.58 EndZ=0
    g6: LineSegment StartX=-10.5834 StartY=-97.5802 StartZ=0 EndX=-10.5834 EndY=-39.7445 EndZ=0
    g7: LineSegment StartX=-13.5834 StartY=-36.7445 StartZ=0 EndX=-53.5834 EndY=-36.7445 EndZ=0
    g8: ArcOfCircle CenterX=-13.5834 CenterY=-39.7445 CenterZ=0 NormalX=0 NormalY=0 NormalZ=1 AngleXU=0 Radius=3 StartAngle=1e-15 EndAngle=1.5708
    g9: ArcOfCircle CenterX=-13.5834 CenterY=6.25546 CenterZ=0 NormalX=0 NormalY=0 NormalZ=1 AngleXU=0 Radius=3 StartAngle=4.71239 EndAngle=6.28319
    g10: ArcOfCircle CenterX=-7.5834 CenterY=27.0662 CenterZ=0 NormalX=0 NormalY=0 NormalZ=1 AngleXU=0 Radius=3 StartAngle=1.5708 EndAngle=3.14159
    g11: ArcOfCircle CenterX=67.0566 CenterY=-97.5802 CenterZ=0 NormalX=0 NormalY=0 NormalZ=1 AngleXU=0 Radius=3 StartAngle=4.71239 EndAngle=6.28319
    g12: ArcOfCircle CenterX=-7.5834 CenterY=-97.5802 CenterZ=0 NormalX=0 NormalY=0 NormalZ=1 AngleXU=0 Radius=3 StartAngle=3.14159 EndAngle=4.71239
  constraints (32):
    c: Horizontal(g1)
    c: Vertical(g2)
    c: Horizontal(g3)
    c: Vertical(g4)
    c: Horizontal(g5)
    c: Vertical(g6)
    c: Horizontal(g7)
    c: Tangent(g6,g8) = -1.5708
    c: Tangent(g7,g8) = -1.5708
    c: Tangent(g1,g9) = -1.5708
    c: Tangent(g2,g9) = -1.5708
    c: Tangent(g2,g10) = 1.5708
    c: Tangent(g3,g10) = 1.5708
    c: Tangent(g4,g11) = 1.5708
    c: Tangent(g5,g11) = 1.5708
    c: Tangent(g5,g12) = 1.5708
    c: Tangent(g6,g12) = 1.5708
    c: Radius(g12) = 3
    c: Equal(g12,g11)
    c: Equal(g10,g9)
    c: DistanceY(g7,g1) = 40
    c: Equal(g1,g7)
    c: DistanceX(g6,g4) = 80.64
    c: Horizontal(g0,g1)
    c: Vertical(g1,g0)
    c: Horizontal(g0,g7)
    c: Vertical(g0)
    c: Block(g0)
    c: Vertical(g7,g0)
    c: Equal(g8,g9)
    c: DistanceX(g1,g1) = 40
    c: Coincident(g3,g4)
FEATURE [PartDesign::Pad] Pad005
  Direction = (1,1,1)
  Length = 6
  Length2 = 100
  Profile = -> Sketch
  Type = 0
FEATURE [Sketcher::SketchObject] Sketch025  label="y-plate-x-axis-mount-threaded-holes"
  ExternalGeometry = -> [Sketch]
  FullyConstrained = true
  MapMode = 5
  Placement = pos=(0,0,6) rot=(0,0,1;0rad)
  Support = -> [Pad005]
  sketch-geometry (5):
    g0: Circle CenterX=-43.5834 CenterY=-6.74454 CenterZ=0 NormalX=0 NormalY=0 NormalZ=1 AngleXU=0 Radius=2.55
    g1: Circle CenterX=-43.5834 CenterY=-26.7445 CenterZ=0 NormalX=0 NormalY=0 NormalZ=1 AngleXU=0 Radius=2.55
    g2: LineSegment StartX=-43.5834 StartY=-6.74454 StartZ=0 EndX=-43.5834 EndY=-26.7445 EndZ=0
    g3: GeomPoint X=-43.5834 Y=-16.7445 Z=0
    g4: GeomPoint X=-53.5834 Y=-16.7445 Z=0
  constraints (10):
    c: Radius(g0) = 2.55
    c: Equal(g0,g1)
    c: Vertical(g1,g0)
    c: DistanceY(g1,g0) = 20
    c: Coincident(g2,g0)
    c: Coincident(g2,g1)
    c: DistanceX(g-3,g1) = 10
    c: Symmetric(g2,g2,g3)
    c: Symmetric(g-4,g-4,g4)
    c: Horizontal(g4,g3)
FEATURE [PartDesign::Hole] Hole006  label="ho-y-plate-x-axis-mount-threaded-holes"
  BaseFeature = -> Pad005
  Depth = 25
  DepthType = 0
  Diameter = 4.2
  DrillForDepth = false
  DrillPoint = 1
  DrillPointAngle = 118
  HoleCutCountersinkAngle = 90
  HoleCutCustomValues = false
  HoleCutDepth = 0
  HoleCutDiameter = 6.1
  HoleCutType = 0
  ModelActualThread = false
  Profile = -> Sketch025
  Tapered = false
  TaperedAngle = 90
  ThreadAngle = 60
  ThreadClass = 0
  ThreadCutOffInner = 0.0866025
  ThreadCutOffOuter = 0.173205
  ThreadDirection = 0
  ThreadFit = 1
  ThreadPitch = 0.8
  ThreadSize = 13
  ThreadType = 1
  Threaded = true
FEATURE [Sketcher::SketchObject] Sketch026  label="y-plate-wheel-excentric-holes"
  ExternalGeometry = -> [Sketch025,Sketch]
  FullyConstrained = true
  MapMode = 5
  Placement = pos=(0,0,6) rot=(0,0,1;0rad)
  Support = -> [Hole006]
  sketch-geometry (2):
    g0: Circle CenterX=-0.583397 CenterY=-31.8945 CenterZ=0 NormalX=0 NormalY=0 NormalZ=1 AngleXU=0 Radius=2.55
    g1: Circle CenterX=60.0566 CenterY=-31.8945 CenterZ=0 NormalX=0 NormalY=0 NormalZ=1 AngleXU=0 Radius=2.55
  constraints (6):
    c: Horizontal(g0,g1)
    c: DistanceX(g0,g1) = 60.64
    c: DistanceY(g0,g-3) = 5.15
    c: DistanceX(g-4,g0) = 10
    c: Radius(g0) = 2.55
    c: Equal(g0,g1)
FEATURE [PartDesign::Hole] Hole007
  BaseFeature = -> Hole006
  Depth = 25
  DepthType = 0
  Diameter = 7.2
  DrillForDepth = false
  DrillPoint = 1
  DrillPointAngle = 118
  HoleCutCountersinkAngle = 90
  HoleCutCustomValues = false
  HoleCutDepth = 0
  HoleCutDiameter = 0
  HoleCutType = 0
  ModelActualThread = false
  Profile = -> Sketch026
  Tapered = false
  TaperedAngle = 90
  ThreadAngle = 0
  ThreadClass = 0
  ThreadCutOffInner = 0
  ThreadCutOffOuter = 0
  ThreadDirection = 0
  ThreadFit = 1
  ThreadPitch = 0
  ThreadSize = 0
  ThreadType = 0
  Threaded = false
FEATURE [Sketcher::SketchObject] Sketch027  label="y-plate-wheel-holes"
  ExternalGeometry = -> [Sketch026]
  FullyConstrained = true
  MapMode = 5
  Placement = pos=(0,0,6) rot=(0,0,1;0rad)
  Support = -> [Hole007]
  sketch-geometry (2):
    g0: Circle CenterX=-0.583397 CenterY=-91.8945 CenterZ=0 NormalX=0 NormalY=0 NormalZ=1 AngleXU=0 Radius=3.6
    g1: Circle CenterX=60.0566 CenterY=-91.8945 CenterZ=0 NormalX=0 NormalY=0 NormalZ=1 AngleXU=0 Radius=3.6
  constraints (6):
    c: Radius(g0) = 3.6
    c: Equal(g0,g1)
    c: Horizontal(g0,g1)
    c: Vertical(g0,g-3)
    c: Vertical(g1,g-4)
    c: DistanceY(g0,g-3) = 60
FEATURE [PartDesign::Hole] Hole008
  BaseFeature = -> Hole007
  Depth = 25
  DepthType = 0
  Diameter = 5.3
  DrillForDepth = false
  DrillPoint = 1
  DrillPointAngle = 118
  HoleCutCountersinkAngle = 90
  HoleCutCustomValues = false
  HoleCutDepth = 0
  HoleCutDiameter = 0
  HoleCutType = 0
  ModelActualThread = false
  Profile = -> Sketch027
  Tapered = false
  TaperedAngle = 90
  ThreadAngle = 0
  ThreadClass = 0
  ThreadCutOffInner = 0
  ThreadCutOffOuter = 0
  ThreadDirection = 0
  ThreadFit = 1
  ThreadPitch = 0
  ThreadSize = 13
  ThreadType = 1
  Threaded = false
FEATURE [Sketcher::SketchObject] Sketch028  label="y-plate-nema-mount-holes"
  ExternalGeometry = -> [Sketch026]
  FullyConstrained = true
  MapMode = 5
  Placement = pos=(0,0,6) rot=(0,0,1;0rad)
  Support = -> [Hole008]
  sketch-geometry (8):
    g0: Circle CenterX=14.2366 CenterY=-0.39454 CenterZ=0 NormalX=0 NormalY=0 NormalZ=1 AngleXU=0 Radius=1.75
    g1: Circle CenterX=45.2366 CenterY=-0.39454 CenterZ=0 NormalX=0 NormalY=0 NormalZ=1 AngleXU=0 Radius=1.75
    g2: Circle CenterX=14.2366 CenterY=-31.3945 CenterZ=0 NormalX=0 NormalY=0 NormalZ=1 AngleXU=0 Radius=1.75
    g3: Circle CenterX=45.2366 CenterY=-31.3945 CenterZ=0 NormalX=0 NormalY=0 NormalZ=1 AngleXU=0 Radius=1.75
    g4: LineSegment StartX=14.2366 StartY=-0.39454 StartZ=0 EndX=45.2366 EndY=-31.3945 EndZ=0
    g5: GeomPoint X=29.7366 Y=-15.8945 Z=0
    g6: LineSegment StartX=-0.583397 StartY=-31.8945 StartZ=0 EndX=60.0566 EndY=-31.8945 EndZ=0
    g7: GeomPoint X=29.7366 Y=-31.8945 Z=0
  constraints (18):
    c: Horizontal(g0,g1)
    c: Horizontal(g2,g3)
    c: Vertical(g0,g2)
    c: Vertical(g1,g3)
    c: DistanceX(g0,g1) = 31
    c: DistanceY(g3,g1) = 31
    c: Radius(g0) = 1.75
    c: Equal(g0,g1)
    c: Equal(g1,g3)
    c: Equal(g3,g2)
    c: Coincident(g4,g0)
    c: Coincident(g4,g3)
    c: Symmetric(g4,g4,g5)
    c: Coincident(g6,g-3)
    c: Coincident(g6,g-4)
    c: Symmetric(g6,g6,g7)
    c: Vertical(g7,g5)
    c: DistanceY(g7,g5) = 16
FEATURE [PartDesign::Hole] Hole009
  BaseFeature = -> Hole008
  Depth = 25
  DepthType = 0
  Diameter = 3.2
  DrillForDepth = false
  DrillPoint = 1
  DrillPointAngle = 118
  HoleCutCountersinkAngle = 90
  HoleCutCustomValues = false
  HoleCutDepth = 0
  HoleCutDiameter = 6.1
  HoleCutType = 0
  ModelActualThread = false
  Profile = -> Sketch028
  Tapered = false
  TaperedAngle = 90
  ThreadAngle = 0
  ThreadClass = 0
  ThreadCutOffInner = 0
  ThreadCutOffOuter = 0
  ThreadDirection = 0
  ThreadFit = 1
  ThreadPitch = 0
  ThreadSize = 9
  ThreadType = 1
  Threaded = false
FEATURE [Sketcher::SketchObject] Sketch029  label="y-plate-nema-central-hole"
  ExternalGeometry = -> [Sketch028]
  FullyConstrained = true
  MapMode = 5
  Placement = pos=(0,0,6) rot=(0,0,1;0rad)
  Support = -> [Hole009]
  sketch-geometry (3):
    g0: Circle CenterX=29.7366 CenterY=-15.8945 CenterZ=0 NormalX=0 NormalY=0 NormalZ=1 AngleXU=0 Radius=12.5
    g1: LineSegment StartX=14.2366 StartY=-0.39454 StartZ=0 EndX=45.2366 EndY=-31.3945 EndZ=0
    g2: GeomPoint X=29.7366 Y=-15.8945 Z=0
  constraints (5):
    c: Radius(g0) = 12.5
    c: Coincident(g1,g-3)
    c: Coincident(g1,g-4)
    c: Symmetric(g1,g1,g2)
    c: Coincident(g2,g0)
FEATURE [PartDesign::Pocket] Pocket001
  BaseFeature = -> Hole009
  Length = 5
  Length2 = 100
  Profile = -> Sketch029
  Type = 1
FEATURE [Part::Feature] Part__Feature127  label="Left Nema 17 Stepper Motor"
  Placement = pos=(-6,253.2,165.8) rot=(0,1,0;1.5708rad)
  shape: bbox 72 x 42.42 x 42.42 mm, 64 faces (baked)
  expr: .Placement.Base.y = Spreadsheet.y_axis_pos - 29.8
FEATURE [PartDesign::FeatureBase] Clone006
  BaseFeature = -> Part__Feature127
  Placement = pos=(-6,333.3,165.8) rot=(0,1,0;1.5708rad)
FEATURE [PartDesign::Body] Body015  label="Right Nema 17 Stepper Motor"
  BaseFeature = -> Part__Feature127
  Group = -> [Clone006]
  Origin = -> Origin019
  Placement = pos=(1000,586.4,0) rot=(0,0,1;3.14159rad)
  Tip = -> Clone006
  expr: .Placement.Base.y = Spreadsheet.y_axis_pos + 303.4
FEATURE [Part::Feature] Part__Feature107001  label="V-Slot 20x40x1000 Linear Rail001"
  Placement = pos=(0,232.9,201.8) rot=(0,1,0;1.5708rad)
  shape: bbox 1000 x 40 x 20 mm, 116 faces (baked)
  expr: .Placement.Base.y = Spreadsheet.y_axis_pos - 50.1
FEATURE [Part::Feature] Part__Feature107003  label="Backplate"
  Placement = pos=(6,-21.0306,-20.9693) rot=(-0.00073,-0.999999,0.00073;1.5708rad)
  shape: bbox 9.006 x 42.06 x 42.06 mm, 160 faces (baked)
FEATURE [Part::Feature] Part__Feature107004  label="Component2"
  Placement = pos=(9,-20.9693,21.0306) rot=(-0.00073,0.999999,-0.00073;1.5708rad)
  shape: bbox 10 x 42.05 x 42.05 mm, 105 faces (baked)
FEATURE [Part::Feature] Part__Feature107005  label="Component4"
  shape: bbox 17 x 6 x 17 mm, 12 faces (baked)
FEATURE [Part::Feature] Part__Feature107006  label="Component5"
  Placement = pos=(0,0,0) rot=(0,-1,0;0.00146rad)
  shape: bbox 8.002 x 6.002 x 8.002 mm, 11 faces (baked)
FEATURE [App::Part] Ballbaring_606RS_v3  label="Ballbaring 606RS v3"
  Group = -> [Part__Feature107005,Part__Feature107006]
  Origin = -> Origin026
  Placement = pos=(16,0,-3.3e-15) rot=(-0.577631,0.577631,0.576788;2.09524rad)
FEATURE [Part::Feature] Part__Feature107007  label="Component7"
  shape: bbox 17 x 6 x 17 mm, 12 faces (baked)
FEATURE [Part::Feature] Part__Feature107008  label="Component8"
  shape: bbox 8.002 x 6.002 x 8.002 mm, 11 faces (baked)
FEATURE [App::Part] Ballbaring_606RS_v3__1_  label="Ballbaring 606RS v3 (1)"
  Group = -> [Part__Feature107007,Part__Feature107008]
  Origin = -> Origin027
  Placement = pos=(-1,1.83e-14,-5.84e-14) rot=(0.577631,0.577631,0.576788;4.18795rad)
FEATURE [Part::Feature] Part__Feature107009  label="Connection"
  Placement = pos=(2.5,18.9941,-4.02773) rot=(0,0.707623,0.70659;3.14159rad)
  shape: bbox 5 x 2.51 x 8.003 mm, 19 faces (baked)
FEATURE [Part::Feature] Part__Feature107010  label="coil outer"
  Placement = pos=(12.75,-21.0306,-20.9693) rot=(-0.00073,-0.999999,0.00073;1.5708rad)
  shape: bbox 10.5 x 42.86 x 42.86 mm, 1210 faces, 22 solids (baked)
FEATURE [Part::Feature] Part__Feature107011  label="drive shaft"
  shape: bbox 40 x 28.68 x 28.68 mm, 11 faces (baked)
FEATURE [Part::Feature] Part__Feature107012  label="90234A308"
  Placement = pos=(46.65,15.5226,15.4774) rot=(-0.00073,-0.999999,0.00073;1.5708rad)
  shape: bbox 14.55 x 6.064 x 6.064 mm, 93 faces (baked)
FEATURE [Part::Feature] Part__Feature107013  label="90234A308 (1)"
  Placement = pos=(46.65,15.4774,-15.5226) rot=(-0.00073,-0.999999,0.00073;1.5708rad)
  shape: bbox 14.55 x 6.064 x 6.064 mm, 93 faces (baked)
FEATURE [Part::Feature] Part__Feature107014  label="90234A308 (2)"
  Placement = pos=(46.65,-15.4774,15.5226) rot=(-0.00073,-0.999999,0.00073;1.5708rad)
  shape: bbox 14.55 x 6.064 x 6.064 mm, 93 faces (baked)
FEATURE [Part::Feature] Part__Feature107015  label="90234A308 (3)"
  Placement = pos=(46.65,-15.5226,-15.4774) rot=(-0.00073,-0.999999,0.00073;1.5708rad)
  shape: bbox 14.55 x 6.064 x 6.064 mm, 93 faces (baked)
FEATURE [App::Part] Component12
  Group = -> [Part__Feature107012,Part__Feature107013,Part__Feature107014,Part__Feature107015]
  Origin = -> Origin028
  Placement = pos=(-35,0,0) rot=(0,0,1;0rad)
FEATURE [App::Part] Steppermotor_NEMA17_1A_1_8___13Ncm_v2  label="Steppermotor NEMA17 1A 1.8° 13Ncm v2"
  Group = -> [Part__Feature107003,Part__Feature107004,Ballbaring_606RS_v3,Ballbaring_606RS_v3__1_,Part__Feature107009,Part__Feature107010,Part__Feature107011,Component12]
  Origin = -> Origin029
  Placement = pos=(0,0,23) rot=(0,-1,0;1.5708rad)
FEATURE [PartDesign::SubShapeBinder] Binder003
  BindMode = 0
  ClaimChildren = false
  Context = -> Part001 [Body018.Binder003.]
  Fuse = false
  MakeFace = true
  PartialLoad = false
  Relative = true
  Support = -> [Body019[Hole026.]]
  _Version = 2
FEATURE [PartDesign::SubShapeBinder] Binder004
  BindMode = 0
  ClaimChildren = false
  Context = -> Part001 [Body018.Binder004.]
  Fuse = false
  MakeFace = true
  PartialLoad = false
  Relative = true
  Support = -> [Body019[Hole027.]]
  _Version = 2
FEATURE [Part::Feature] Part__Feature107016  label="Nema 17 Stepper Motor002"
  Placement = pos=(0,-31.5,0) rot=(0,0,1;0rad)
  shape: bbox 42.42 x 42.42 x 72 mm, 64 faces (baked)
FEATURE [Part::Feature] Part__Feature  label="ELP-USBFHD01M-L21"
  Placement = pos=(0,-107,23) rot=(0,0,1;3.14159rad)
  shape: bbox 38.04 x 27.94 x 38.04 mm, 666 faces, 0 solids (baked)
FEATURE [Part::Feature] Part__Feature107017  label="Xtreme Solid V Wheel"
  shape: bbox 10.2 x 23.9 x 23.9 mm, 16 faces (baked)
FEATURE [Part::Feature] Part__Feature107017_cs
  shape: bbox 2e-07 x 23.9 x 23.9 mm, 0 faces, 0 solids (baked)
FEATURE [Sketcher::SketchObject] Sketch061
  FullyConstrained = false
  Placement = pos=(0,0,0) rot=(0,1,0;1.5708rad)
  sketch-geometry (4):
    g0: ArcOfCircle CenterX=0 CenterY=1e-16 CenterZ=0 NormalX=1e-16 NormalY=0 NormalZ=1 AngleXU=0 Radius=11.95 StartAngle=3.14159 EndAngle=6.28319
    g1: ArcOfCircle CenterX=0 CenterY=0 CenterZ=0 NormalX=1e-16 NormalY=0 NormalZ=1 AngleXU=0 Radius=11.95 StartAngle=4e-16 EndAngle=3.14159
    g2: ArcOfCircle CenterX=0 CenterY=1e-16 CenterZ=0 NormalX=1e-16 NormalY=0 NormalZ=1 AngleXU=0 Radius=7 StartAngle=3.14159 EndAngle=6.28319
    g3: ArcOfCircle CenterX=0 CenterY=0 CenterZ=0 NormalX=1e-16 NormalY=0 NormalZ=1 AngleXU=0 Radius=7 StartAngle=1e-16 EndAngle=3.14159
  constraints (4):
    c: Coincident(g0,g1)
    c: Coincident(g1,g0)
    c: Coincident(g2,g3)
    c: Coincident(g3,g2)
FEATURE [PartDesign::SubShapeBinder] Binder
  BindMode = 0
  ClaimChildren = false
  Context = -> Part001 [Body018.Binder.]
  Fuse = false
  MakeFace = true
  PartialLoad = false
  Relative = true
  Support = -> [Body019[Hole031.]]
  _Version = 2
FEATURE [App::Link] Link  label="Head001"
  LinkPlacement = pos=(500,329.4,242) rot=(1,0,0;1.5708rad)
  LinkedObject = -> Part001
  Placement = pos=(500,329.4,242) rot=(1,0,0;1.5708rad)
  expr: .Placement.Base.y = Spreadsheet.y_axis_pos + 46.4
FEATURE [App::DocumentObjectGroup] Group006  label="X-Axis"
  Group = -> [Part__Feature107,Part__Feature127,Body013,Body012,Body014,Body015,Part__Feature107001]
FEATURE [App::DocumentObjectGroup] Group007  label="Machine"
  Group = -> [Group,Body005,Group006,ed1_board_support,Link]
FEATURE [PartDesign::Body] Body012  label="X-Axis Plate"
  Group = -> [Sketch,Sketch025,Sketch026,Pad005,Hole006,Hole007,Sketch027,Hole008,Sketch028,Sketch029,Hole009,Pocket001,Sketch030,Hole010,Sketch031,Hole011,Sketch032,Hole012,Sketch033,Pocket]
  Origin = -> Origin016
  Tip = -> Pocket
FEATURE [PartDesign::Body] Body013  label="X-Axis Left Plate"
  BaseFeature = -> Body012
  Group = -> [Clone004]
  Origin = -> Origin017
  Placement = pos=(0,283,181.7) rot=(0.57735,-0.57735,-0.57735;2.0944rad)
  Tip = -> Clone004
  expr: .Placement.Base.y = Spreadsheet.y_axis_pos
FEATURE [PartDesign::FeatureBase] Clone004
  BaseFeature = -> Body012
FEATURE [Sketcher::SketchObject] Sketch030  label="y-plate-drag-chain-support"
  ExternalGeometry = -> [Sketch]
  FullyConstrained = false
  MapMode = 5
  Placement = pos=(0,0,0) rot=(1,0,0;3.14159rad)
  Support = -> [Clone004]
  sketch-geometry (3):
    g0: Circle CenterX=40.0566 CenterY=-20.1055 CenterZ=0 NormalX=0 NormalY=0 NormalZ=1 AngleXU=0 Radius=2.5
    g1: Circle CenterX=60.0566 CenterY=-20.1055 CenterZ=0 NormalX=0 NormalY=0 NormalZ=1 AngleXU=0 Radius=2.5
    g2: LineSegment StartX=40.0566 StartY=-20.1055 StartZ=0 EndX=60.0566 EndY=-20.1055 EndZ=0
  constraints (7):
    c: Radius(g0) = 2.5
    c: Equal(g0,g1)
    c: Horizontal(g0,g1)
    c: DistanceX(g0,g1) = 20
    c: Coincident(g2,g0)
    c: Coincident(g2,g1)
    c: DistanceX(g1,g-3) = 10
FEATURE [PartDesign::Hole] Hole010
  BaseFeature = -> Pocket001
  Depth = 25
  DepthType = 0
  Diameter = 5.3
  DrillForDepth = false
  DrillPoint = 1
  DrillPointAngle = 118
  HoleCutCountersinkAngle = 90
  HoleCutCustomValues = false
  HoleCutDepth = 0
  HoleCutDiameter = 6.1
  HoleCutType = 0
  ModelActualThread = false
  Profile = -> Sketch030
  Tapered = false
  TaperedAngle = 90
  ThreadAngle = 0
  ThreadClass = 0
  ThreadCutOffInner = 0
  ThreadCutOffOuter = 0
  ThreadDirection = 0
  ThreadFit = 1
  ThreadPitch = 0
  ThreadSize = 13
  ThreadType = 1
  Threaded = false
FEATURE [Sketcher::SketchObject] Sketch031  label="y-plate-x-axis-mount-holes"
  ExternalGeometry = -> [Sketch025]
  FullyConstrained = true
  MapMode = 5
  Placement = pos=(0,0,6) rot=(0,0,1;0rad)
  Support = -> [Hole010]
  sketch-geometry (2):
    g0: Circle CenterX=-23.5834 CenterY=-6.74454 CenterZ=0 NormalX=0 NormalY=0 NormalZ=1 AngleXU=0 Radius=2.55
    g1: Circle CenterX=-23.5834 CenterY=-26.7445 CenterZ=0 NormalX=0 NormalY=0 NormalZ=1 AngleXU=0 Radius=2.55
  constraints (6):
    c: Equal(g1,g0)
    c: Equal(g0,g-4)
    c: Horizontal(g-3,g0)
    c: Horizontal(g-4,g1)
    c: Vertical(g1,g0)
    c: DistanceX(g-3,g0) = 20
FEATURE [PartDesign::Hole] Hole011  label="ho-y-plate-x-axis-mount-holes"
  BaseFeature = -> Hole010
  Depth = 25
  DepthType = 0
  Diameter = 5.3
  DrillForDepth = false
  DrillPoint = 1
  DrillPointAngle = 118
  HoleCutCountersinkAngle = 90
  HoleCutCustomValues = false
  HoleCutDepth = 0
  HoleCutDiameter = 6.1
  HoleCutType = 0
  ModelActualThread = false
  Profile = -> Sketch031
  Tapered = false
  TaperedAngle = 90
  ThreadAngle = 60
  ThreadClass = 0
  ThreadCutOffInner = 0.0866025
  ThreadCutOffOuter = 0.173205
  ThreadDirection = 1
  ThreadFit = 1
  ThreadPitch = 0.8
  ThreadSize = 13
  ThreadType = 1
  Threaded = false
FEATURE [Sketcher::SketchObject] Sketch032  label="y-plate-drag-mount-hole"
  ExternalGeometry = -> [Sketch027,Sketch]
  FullyConstrained = true
  MapMode = 5
  Placement = pos=(0,0,6) rot=(0,0,1;0rad)
  Support = -> [Hole011]
  sketch-geometry (3):
    g0: Circle CenterX=29.7366 CenterY=-75.5802 CenterZ=0 NormalX=0 NormalY=0 NormalZ=1 AngleXU=0 Radius=2.5
    g1: LineSegment StartX=-0.583397 StartY=-91.8945 StartZ=0 EndX=60.0566 EndY=-91.8945 EndZ=0
    g2: GeomPoint X=29.7366 Y=-91.8945 Z=0
  constraints (6):
    c: Radius(g0) = 2.5
    c: DistanceY(g-4,g0) = 25
    c: Coincident(g1,g-5)
    c: Coincident(g1,g-3)
    c: Symmetric(g1,g1,g2)
    c: Vertical(g2,g0)
FEATURE [PartDesign::Hole] Hole012
  BaseFeature = -> Hole011
  Depth = 25
  DepthType = 0
  Diameter = 4.2
  DrillForDepth = false
  DrillPoint = 1
  DrillPointAngle = 118
  HoleCutCountersinkAngle = 90
  HoleCutCustomValues = false
  HoleCutDepth = 0
  HoleCutDiameter = 6.1
  HoleCutType = 0
  ModelActualThread = false
  Profile = -> Sketch032
  Tapered = false
  TaperedAngle = 90
  ThreadAngle = 60
  ThreadClass = 0
  ThreadCutOffInner = 0.0866025
  ThreadCutOffOuter = 0.173205
  ThreadDirection = 0
  ThreadFit = 0
  ThreadPitch = 0.8
  ThreadSize = 13
  ThreadType = 1
  Threaded = true
FEATURE [Sketcher::SketchObject] Sketch033  label="y-plate-x-axis-cable-hole"
  ExternalGeometry = -> [Sketch025]
  FullyConstrained = true
  MapMode = 5
  Placement = pos=(0,0,6) rot=(0,0,1;0rad)
  Support = -> [Hole012]
  sketch-geometry (3):
    g0: Circle CenterX=-23.5834 CenterY=-16.7445 CenterZ=0 NormalX=0 NormalY=0 NormalZ=1 AngleXU=0 Radius=4.21
    g1: LineSegment StartX=-43.5834 StartY=-6.74454 StartZ=0 EndX=-43.5834 EndY=-26.7445 EndZ=0
    g2: GeomPoint X=-43.5834 Y=-16.7445 Z=0
  constraints (6):
    c: Radius(g0) = 4.21
    c: Coincident(g1,g-3)
    c: Coincident(g1,g-4)
    c: Symmetric(g1,g1,g2)
    c: Horizontal(g2,g0)
    c: DistanceX(g2,g0) = 20
FEATURE [PartDesign::Pocket] Pocket  label="po-y-plate-x-axis-cable-hole"
  BaseFeature = -> Hole012
  Length = 5
  Length2 = 100
  Profile = -> Sketch033
  Type = 1
FEATURE [PartDesign::Body] Body014  label="X-Axis Right Plate"
  BaseFeature = -> Body013
  Group = -> [Clone005]
  Origin = -> Origin018
  Placement = pos=(1000,586.4,0) rot=(0,0,1;3.14159rad)
  Tip = -> Clone005
  expr: .Placement.Base.y = Spreadsheet.y_axis_pos + 303.4
FEATURE [PartDesign::FeatureBase] Clone005
  BaseFeature = -> Body013
  Placement = pos=(-6,303.6,181.7) rot=(0.57735,0.57735,0.57735;2.0944rad)
FEATURE [App::Part] Part001  label="Head"
  Group = -> [Body018,Body019,Steppermotor_NEMA17_1A_1_8___13Ncm_v2,Part__Feature107016,Part__Feature]
  Origin = -> Origin023
FEATURE [PartDesign::Body] Body018  label="Head Back"
  Group = -> [Sketch047,Sketch048,Sketch049,Sketch050,Binder003,Binder004,Sketch060,Pad010,Hole028,Pocket006,Hole029,Hole030,Sketch063,Binder,Hole032]
  Origin = -> Origin024
  Tip = -> Hole032
FEATURE [PartDesign::Body] Body019  label="Head Front"
  Group = -> [Sketch051,Sketch052,Sketch054,Sketch056,Sketch057,Sketch058,Sketch059,Pad009,Hole023,Pocket005,Hole024,Hole025,Hole026,Hole027,Sketch062,Hole031]
  Origin = -> Origin025
  Placement = pos=(0,0,40) rot=(0,0,1;0rad)
  Tip = -> Hole031
FEATURE [Sketcher::SketchObject] Sketch047  label="head-back-nema-mount-holes"
  FullyConstrained = true
  MapMode = 5
  Placement = pos=(0,0,6) rot=(0,0,1;0rad)
  Support = -> [Pad010]
  sketch-geometry (6):
    g0: Circle CenterX=-15.5 CenterY=-16 CenterZ=0 NormalX=0 NormalY=0 NormalZ=1 AngleXU=0 Radius=1.5
    g1: Circle CenterX=-15.5 CenterY=-47 CenterZ=0 NormalX=0 NormalY=0 NormalZ=1 AngleXU=0 Radius=1.5
    g2: Circle CenterX=15.5 CenterY=-16 CenterZ=0 NormalX=0 NormalY=0 NormalZ=1 AngleXU=0 Radius=1.5
    g3: Circle CenterX=15.5 CenterY=-47 CenterZ=0 NormalX=0 NormalY=0 NormalZ=1 AngleXU=0 Radius=1.5
    g4: LineSegment StartX=-15.5 StartY=-16 StartZ=0 EndX=15.5 EndY=-47 EndZ=0
    g5: GeomPoint X=-1.1e-15 Y=-31.5 Z=0
  constraints (15):
    c: Radius(g0) = 1.5
    c: Equal(g0,g2)
    c: Equal(g2,g3)
    c: Equal(g3,g1)
    c: Horizontal(g0,g2)
    c: Horizontal(g1,g3)
    c: Vertical(g0,g1)
    c: Vertical(g2,g3)
    c: DistanceX(g0,g2) = 31
    c: DistanceY(g1,g0) = 31
    c: Coincident(g4,g0)
    c: Coincident(g4,g3)
    c: Symmetric(g4,g4,g5)
    c: Vertical(g5,g-1)
    c: DistanceY(g5,g-1) = 31.5
FEATURE [Sketcher::SketchObject] Sketch048  label="head-back-excentric-wheel-holes"
  ExternalGeometry = -> [Binder003]
  FullyConstrained = false
  MapMode = 5
  Placement = pos=(0,0,6) rot=(0,0,1;0rad)
  Support = -> [Pocket006]
  sketch-geometry (2):
    g0: Circle CenterX=31 CenterY=-47 CenterZ=0 NormalX=0 NormalY=0 NormalZ=1 AngleXU=0 Radius=2.80181
    g1: Circle CenterX=-31 CenterY=-47 CenterZ=0 NormalX=0 NormalY=0 NormalZ=1 AngleXU=0 Radius=2.80181
  constraints (1):
    c: Equal(g1,g0)
FEATURE [Sketcher::SketchObject] Sketch049  label="head-back-wheel-holes"
  ExternalGeometry = -> [Sketch048,Binder004]
  FullyConstrained = true
  MapMode = 5
  Placement = pos=(0,0,6) rot=(0,0,1;0rad)
  Support = -> [Hole029]
  sketch-geometry (2):
    g0: Circle CenterX=-31 CenterY=-107 CenterZ=0 NormalX=0 NormalY=0 NormalZ=1 AngleXU=0 Radius=2.65
    g1: Circle CenterX=31 CenterY=-107 CenterZ=0 NormalX=0 NormalY=0 NormalZ=1 AngleXU=0 Radius=2.65
  constraints (4):
    c: Equal(g-5,g0)
    c: Equal(g0,g1)
    c: Coincident(g0,g-5)
    c: Coincident(g1,g-6)
FEATURE [Sketcher::SketchObject] Sketch050  label="head-back-nema-central-holes"
  ExternalGeometry = -> [Sketch047]
  FullyConstrained = false
  MapMode = 5
  Placement = pos=(0,0,6) rot=(0,0,1;0rad)
  Support = -> [Hole028]
  sketch-geometry (3):
    g0: LineSegment StartX=-15.5 StartY=-16 StartZ=0 EndX=15.5 EndY=-47 EndZ=0
    g1: GeomPoint X=9e-16 Y=-31.5 Z=0
    g2: Circle CenterX=9e-16 CenterY=-31.5 CenterZ=0 NormalX=0 NormalY=0 NormalZ=1 AngleXU=0 Radius=12.5
  constraints (3):
    c: Symmetric(g0,g0,g1)
    c: Coincident(g2,g1)
    c: Radius(g2) = 12.5
FEATURE [Sketcher::SketchObject] Sketch051  label="head-front-nema-mount-holes"
  FullyConstrained = true
  MapMode = 5
  Placement = pos=(0,0,6) rot=(0,0,1;0rad)
  Support = -> [Pad009]
  sketch-geometry (6):
    g0: Circle CenterX=-15.5 CenterY=15.5 CenterZ=0 NormalX=0 NormalY=0 NormalZ=1 AngleXU=0 Radius=2.5
    g1: Circle CenterX=15.5 CenterY=15.5 CenterZ=0 NormalX=0 NormalY=0 NormalZ=1 AngleXU=0 Radius=2.5
    g2: Circle CenterX=-15.5 CenterY=-15.5 CenterZ=0 NormalX=0 NormalY=0 NormalZ=1 AngleXU=0 Radius=2.5
    g3: Circle CenterX=15.5 CenterY=-15.5 CenterZ=0 NormalX=0 NormalY=0 NormalZ=1 AngleXU=0 Radius=2.5
    g4: LineSegment StartX=-15.5 StartY=15.5 StartZ=0 EndX=15.5 EndY=-15.5 EndZ=0
    g5: GeomPoint X=-1e-16 Y=-1e-16 Z=0
  constraints (14):
    c: Radius(g0) = 2.5
    c: Equal(g0,g1)
    c: Equal(g1,g3)
    c: Equal(g3,g2)
    c: Vertical(g0,g2)
    c: Vertical(g1,g3)
    c: Horizontal(g0,g1)
    c: Horizontal(g2,g3)
    c: DistanceX(g0,g1) = 31
    c: DistanceY(g3,g1) = 31
    c: Coincident(g4,g0)
    c: Coincident(g4,g3)
    c: Symmetric(g4,g4,g5)
    c: Coincident(g5,g-1)
FEATURE [Sketcher::SketchObject] Sketch052  label="head-front-nema-central-holes"
  ExternalGeometry = -> [Sketch051]
  FullyConstrained = true
  MapMode = 5
  Placement = pos=(0,0,6) rot=(0,0,1;0rad)
  Support = -> [Hole023]
  sketch-geometry (3):
    g0: LineSegment StartX=-15.5 StartY=15.5 StartZ=0 EndX=15.5 EndY=-15.5 EndZ=0
    g1: GeomPoint X=-4e-16 Y=4e-16 Z=0
    g2: Circle CenterX=-4e-16 CenterY=4e-16 CenterZ=0 NormalX=0 NormalY=0 NormalZ=1 AngleXU=0 Radius=12.5
  constraints (5):
    c: Coincident(g0,g-3)
    c: Coincident(g0,g-4)
    c: Symmetric(g0,g0,g1)
    c: Coincident(g2,g1)
    c: Radius(g2) = 12.5
FEATURE [Sketcher::SketchObject] Sketch054  label="head-front-nozzle-lift-transmission-pulley"
  ExternalGeometry = -> [Sketch057]
  FullyConstrained = true
  MapMode = 5
  Placement = pos=(0,0,6) rot=(0,0,1;0rad)
  Support = -> [Hole024]
  sketch-geometry (1):
    g0: Circle CenterX=0 CenterY=-129 CenterZ=0 NormalX=0 NormalY=0 NormalZ=1 AngleXU=0 Radius=1.5
  constraints (3):
    c: Radius(g0) = 1.5
    c: Vertical(g0,g-1)
    c: DistanceY(g0,g-3) = 16
FEATURE [Sketcher::SketchObject] Sketch056  label="head-front-wheel-holes"
  ExternalGeometry = -> [Sketch058]
  FullyConstrained = false
  MapMode = 5
  Placement = pos=(0,0,6) rot=(0,0,1;0rad)
  Support = -> [Hole026]
  sketch-geometry (3):
    g0: Circle CenterX=-31 CenterY=-107 CenterZ=0 NormalX=0 NormalY=0 NormalZ=1 AngleXU=0 Radius=2.5
    g1: Circle CenterX=31 CenterY=-107 CenterZ=0 NormalX=0 NormalY=0 NormalZ=1 AngleXU=0 Radius=2.5
    g2: Circle CenterX=-31 CenterY=-107 CenterZ=0 NormalX=0 NormalY=0 NormalZ=1 AngleXU=0 Radius=5.975
  constraints (6):
    c: Horizontal(g0,g1)
    c: Vertical(g-3,g0)
    c: Vertical(g-4,g1)
    c: DistanceY(g0,g-3) = 60
    c: Coincident(g2,g0)
    c: Radius(g2) = 5.975
FEATURE [Sketcher::SketchObject] Sketch057  label="head-front-hiwin-rails-mount-holes"
  FullyConstrained = false
  MapMode = 5
  Placement = pos=(0,0,6) rot=(0,0,1;0rad)
  Support = -> [Pocket005]
  sketch-geometry (11):
    g0: Circle CenterX=-13 CenterY=-53 CenterZ=0 NormalX=0 NormalY=0 NormalZ=1 AngleXU=0 Radius=1.5
    g1: Circle CenterX=-13 CenterY=-73 CenterZ=0 NormalX=0 NormalY=0 NormalZ=1 AngleXU=0 Radius=1.5
    g2: Circle CenterX=-13 CenterY=-93 CenterZ=0 NormalX=0 NormalY=0 NormalZ=1 AngleXU=0 Radius=1.5
    g3: Circle CenterX=-13 CenterY=-113 CenterZ=0 NormalX=0 NormalY=0 NormalZ=1 AngleXU=0 Radius=1.5
    g4: Circle CenterX=13 CenterY=-53 CenterZ=0 NormalX=0 NormalY=0 NormalZ=1 AngleXU=0 Radius=1.5
    g5: Circle CenterX=13 CenterY=-73 CenterZ=0 NormalX=0 NormalY=0 NormalZ=1 AngleXU=0 Radius=1.5
    g6: Circle CenterX=13 CenterY=-93 CenterZ=0 NormalX=0 NormalY=0 NormalZ=1 AngleXU=0 Radius=1.5
    g7: Circle CenterX=13 CenterY=-113 CenterZ=0 NormalX=0 NormalY=0 NormalZ=1 AngleXU=0 Radius=1.5
    g8: LineSegment StartX=-13 StartY=-53 StartZ=0 EndX=13 EndY=-53 EndZ=0
    g9: GeomPoint X=-2.864e-13 Y=-53 Z=0
    g10: LineSegment StartX=-17.5 StartY=-32.6577 StartZ=0 EndX=-17.5 EndY=-70.9981 EndZ=0
  constraints (29):
    c: Equal(g0,g1)
    c: Equal(g1,g2)
    c: Equal(g2,g3)
    c: Equal(g3,g4)
    c: Equal(g4,g5)
    c: Equal(g5,g6)
    c: Equal(g6,g7)
    c: Radius(g0) = 1.5
    c: Horizontal(g0,g4)
    c: Horizontal(g1,g5)
    c: Horizontal(g2,g6)
    c: Horizontal(g3,g7)
    c: Vertical(g4,g5)
    c: Vertical(g5,g6)
    c: Vertical(g6,g7)
    c: Vertical(g3,g2)
    c: Vertical(g2,g1)
    c: Vertical(g1,g0)
    c: DistanceX(g0,g4) = 26
    c: DistanceY(g1,g0) = 20
    c: DistanceY(g3,g2) = 20
    c: DistanceY(g2,g1) = 20
    c: Coincident(g8,g0)
    c: Coincident(g8,g4)
    c: Symmetric(g8,g8,g9)
    c: Vertical(g9,g-1)
    c: DistanceY(g7,g-1) = 113
    c: Vertical(g10)
    c: DistanceX(g10,g0) = 4.5
FEATURE [Sketcher::SketchObject] Sketch058  label="head-front-excentric-wheel-holes"
  FullyConstrained = true
  MapMode = 5
  Placement = pos=(0,0,6) rot=(0,0,1;0rad)
  Support = -> [Hole025]
  sketch-geometry (2):
    g0: Circle CenterX=-31 CenterY=-47 CenterZ=0 NormalX=0 NormalY=0 NormalZ=1 AngleXU=0 Radius=2.5
    g1: Circle CenterX=31 CenterY=-47 CenterZ=0 NormalX=0 NormalY=0 NormalZ=1 AngleXU=0 Radius=2.5
  constraints (6):
    c: Radius(g0) = 2.5
    c: Horizontal(g0,g1)
    c: Equal(g0,g1)
    c: DistanceX(g0,g-1) = 31
    c: DistanceX(g-1,g1) = 31
    c: DistanceY(g0,g-1) = 47
FEATURE [Sketcher::SketchObject] Sketch059  label="head-front-body"
  ExternalGeometry = -> [Sketch058,Sketch054]
  FullyConstrained = true
  MapMode = 5
  Support = -> [XY_Plane025]
  sketch-geometry (8):
    g0: LineSegment StartX=-38 StartY=22 StartZ=0 EndX=38 EndY=22 EndZ=0
    g1: LineSegment StartX=41 StartY=19 StartZ=0 EndX=41 EndY=-136 EndZ=0
    g2: LineSegment StartX=38 StartY=-139 StartZ=0 EndX=-38 EndY=-139 EndZ=0
    g3: LineSegment StartX=-41 StartY=-136 StartZ=0 EndX=-41 EndY=19 EndZ=0
    g4: ArcOfCircle CenterX=-38 CenterY=19 CenterZ=0 NormalX=0 NormalY=0 NormalZ=1 AngleXU=0 Radius=3 StartAngle=1.5708 EndAngle=3.14159
    g5: ArcOfCircle CenterX=38 CenterY=19 CenterZ=0 NormalX=0 NormalY=0 NormalZ=1 AngleXU=0 Radius=3 StartAngle=4.143e-13 EndAngle=1.5708
    g6: ArcOfCircle CenterX=38 CenterY=-136 CenterZ=0 NormalX=0 NormalY=0 NormalZ=1 AngleXU=0 Radius=3 StartAngle=4.71239 EndAngle=6.28319
    g7: ArcOfCircle CenterX=-38 CenterY=-136 CenterZ=0 NormalX=0 NormalY=0 NormalZ=1 AngleXU=0 Radius=3 StartAngle=3.14159 EndAngle=4.71239
  constraints (20):
    c: Horizontal(g0)
    c: Horizontal(g2)
    c: Vertical(g1)
    c: Vertical(g3)
    c: Tangent(g0,g4) = 1.5708
    c: Tangent(g3,g4) = 1.5708
    c: Tangent(g0,g5) = 1.5708
    c: Tangent(g1,g5) = 1.5708
    c: Tangent(g1,g6) = 1.5708
    c: Tangent(g2,g6) = 1.5708
    c: Tangent(g2,g7) = 1.5708
    c: Tangent(g3,g7) = 1.5708
    c: Radius(g4) = 3
    c: Equal(g4,g5)
    c: Equal(g5,g6)
    c: Equal(g6,g7)
    c: DistanceX(g3,g-3) = 10
    c: DistanceX(g-5,g1) = 10
    c: DistanceY(g2,g-4) = 10
    c: DistanceY(g-1,g0) = 22
FEATURE [PartDesign::Pad] Pad009  label="pd-head-front-body"
  Direction = (1,1,1)
  Length = 6
  Length2 = 100
  Profile = -> Sketch059
  Type = 0
FEATURE [PartDesign::Hole] Hole023  label="ho-head-front-nema-mount-holes"
  BaseFeature = -> Pad009
  Depth = 25
  DepthType = 0
  Diameter = 3.2
  DrillForDepth = false
  DrillPoint = 1
  DrillPointAngle = 118
  HoleCutCountersinkAngle = 90
  HoleCutCustomValues = false
  HoleCutDepth = 0
  HoleCutDiameter = 6.1
  HoleCutType = 0
  ModelActualThread = false
  Profile = -> Sketch051
  Tapered = false
  TaperedAngle = 90
  ThreadAngle = 0
  ThreadClass = 0
  ThreadCutOffInner = 0
  ThreadCutOffOuter = 0
  ThreadDirection = 0
  ThreadFit = 1
  ThreadPitch = 0
  ThreadSize = 9
  ThreadType = 1
  Threaded = false
FEATURE [PartDesign::Pocket] Pocket005  label="po-head-front-nema-central-holes"
  BaseFeature = -> Hole023
  Length = 5
  Length2 = 100
  Profile = -> Sketch052
  Type = 1
FEATURE [PartDesign::Hole] Hole024  label="ho-head-front-hiwin-rails-mount-holes"
  BaseFeature = -> Pocket005
  Depth = 25
  DepthType = 0
  Diameter = 2.5
  DrillForDepth = false
  DrillPoint = 1
  DrillPointAngle = 118
  HoleCutCountersinkAngle = 90
  HoleCutCustomValues = false
  HoleCutDepth = 0
  HoleCutDiameter = 6.1
  HoleCutType = 0
  ModelActualThread = false
  Profile = -> Sketch057
  Tapered = false
  TaperedAngle = 90
  ThreadAngle = 60
  ThreadClass = 0
  ThreadCutOffInner = 0.0541266
  ThreadCutOffOuter = 0.108253
  ThreadDirection = 0
  ThreadFit = 1
  ThreadPitch = 0.5
  ThreadSize = 9
  ThreadType = 1
  Threaded = true
FEATURE [PartDesign::Hole] Hole025  label="ho-head-front-nozzle-lift-transmission-pulley"
  BaseFeature = -> Hole024
  Depth = 25
  DepthType = 0
  Diameter = 2.5
  DrillForDepth = false
  DrillPoint = 1
  DrillPointAngle = 118
  HoleCutCountersinkAngle = 90
  HoleCutCustomValues = false
  HoleCutDepth = 0
  HoleCutDiameter = 6.1
  HoleCutType = 0
  ModelActualThread = false
  Profile = -> Sketch054
  Tapered = false
  TaperedAngle = 90
  ThreadAngle = 60
  ThreadClass = 0
  ThreadCutOffInner = 0.0541266
  ThreadCutOffOuter = 0.108253
  ThreadDirection = 0
  ThreadFit = 1
  ThreadPitch = 0.5
  ThreadSize = 9
  ThreadType = 1
  Threaded = true
FEATURE [PartDesign::Hole] Hole026  label="ho-head-front-excentric-wheel-holes"
  BaseFeature = -> Hole025
  Depth = 25
  DepthType = 0
  Diameter = 7.2
  DrillForDepth = false
  DrillPoint = 1
  DrillPointAngle = 118
  HoleCutCountersinkAngle = 90
  HoleCutCustomValues = false
  HoleCutDepth = 0
  HoleCutDiameter = 6.1
  HoleCutType = 0
  ModelActualThread = false
  Profile = -> Sketch058
  Tapered = false
  TaperedAngle = 90
  ThreadAngle = 0
  ThreadClass = 0
  ThreadCutOffInner = 0
  ThreadCutOffOuter = 0
  ThreadDirection = 0
  ThreadFit = 0
  ThreadPitch = 0
  ThreadSize = 0
  ThreadType = 0
  Threaded = false
FEATURE [PartDesign::Hole] Hole027  label="ho-head-front-wheel-holes"
  BaseFeature = -> Hole026
  Depth = 25
  DepthType = 0
  Diameter = 5.3
  DrillForDepth = false
  DrillPoint = 1
  DrillPointAngle = 118
  HoleCutCountersinkAngle = 90
  HoleCutCustomValues = false
  HoleCutDepth = 0
  HoleCutDiameter = 6.1
  HoleCutType = 0
  ModelActualThread = false
  Profile = -> Sketch056
  Tapered = false
  TaperedAngle = 90
  ThreadAngle = 0
  ThreadClass = 0
  ThreadCutOffInner = 0
  ThreadCutOffOuter = 0
  ThreadDirection = 0
  ThreadFit = 1
  ThreadPitch = 0
  ThreadSize = 13
  ThreadType = 1
  Threaded = false
FEATURE [Sketcher::SketchObject] Sketch060  label="head-back-body"
  ExternalGeometry = -> [Sketch049,Binder003]
  FullyConstrained = false
  MapMode = 5
  Support = -> [XY_Plane024]
  sketch-geometry (8):
    g0: LineSegment StartX=-38 StartY=-8.9852 StartZ=0 EndX=38 EndY=-8.9852 EndZ=0
    g1: LineSegment StartX=41 StartY=-11.9852 StartZ=0 EndX=41 EndY=-119 EndZ=0
    g2: LineSegment StartX=38 StartY=-122 StartZ=0 EndX=-38 EndY=-122 EndZ=0
    g3: LineSegment StartX=-41 StartY=-119 StartZ=0 EndX=-41 EndY=-11.9852 EndZ=0
    g4: ArcOfCircle CenterX=-38 CenterY=-11.9852 CenterZ=0 NormalX=0 NormalY=0 NormalZ=1 AngleXU=0 Radius=3 StartAngle=1.5708 EndAngle=3.14159
    g5: ArcOfCircle CenterX=-38 CenterY=-119 CenterZ=0 NormalX=0 NormalY=0 NormalZ=1 AngleXU=0 Radius=3 StartAngle=3.14159 EndAngle=4.71239
    g6: ArcOfCircle CenterX=38 CenterY=-119 CenterZ=0 NormalX=0 NormalY=0 NormalZ=1 AngleXU=0 Radius=3 StartAngle=4.71239 EndAngle=6.28319
    g7: ArcOfCircle CenterX=38 CenterY=-11.9852 CenterZ=0 NormalX=0 NormalY=0 NormalZ=1 AngleXU=0 Radius=3 StartAngle=7.652e-13 EndAngle=1.5708
  constraints (19):
    c: Horizontal(g0)
    c: Horizontal(g2)
    c: Vertical(g1)
    c: Vertical(g3)
    c: Tangent(g0,g4) = 1.5708
    c: Tangent(g3,g4) = 1.5708
    c: Tangent(g2,g5) = 1.5708
    c: Tangent(g3,g5) = 1.5708
    c: Tangent(g1,g6) = 1.5708
    c: Tangent(g2,g6) = 1.5708
    c: Tangent(g0,g7) = 1.5708
    c: Tangent(g1,g7) = 1.5708
    c: Radius(g4) = 3
    c: Equal(g4,g7)
    c: Equal(g7,g6)
    c: Equal(g6,g5)
    c: DistanceY(g2,g-3) = 15
    c: Vertical(g3,g-4)
    c: Vertical(g1,g-5)
FEATURE [PartDesign::Pad] Pad010  label="pd-head-back-body"
  Direction = (1,1,1)
  Length = 6
  Length2 = 100
  Profile = -> Sketch060
  Type = 0
FEATURE [PartDesign::Hole] Hole028  label="ho-head-back-nema-mount-holes"
  BaseFeature = -> Pad010
  Depth = 25
  DepthType = 0
  Diameter = 3.2
  DrillForDepth = false
  DrillPoint = 1
  DrillPointAngle = 118
  HoleCutCountersinkAngle = 90
  HoleCutCustomValues = false
  HoleCutDepth = 0
  HoleCutDiameter = 6.1
  HoleCutType = 0
  ModelActualThread = false
  Profile = -> Sketch047
  Tapered = false
  TaperedAngle = 90
  ThreadAngle = 0
  ThreadClass = 0
  ThreadCutOffInner = 0
  ThreadCutOffOuter = 0
  ThreadDirection = 0
  ThreadFit = 1
  ThreadPitch = 0
  ThreadSize = 9
  ThreadType = 1
  Threaded = false
FEATURE [PartDesign::Pocket] Pocket006  label="po-head-back-nema-central-holes"
  BaseFeature = -> Hole028
  Length = 5
  Length2 = 100
  Profile = -> Sketch050
  Type = 1
FEATURE [PartDesign::Hole] Hole029  label="ho-head-back-excentric-wheel-holes"
  BaseFeature = -> Pocket006
  Depth = 25
  DepthType = 0
  Diameter = 7.2
  DrillForDepth = false
  DrillPoint = 1
  DrillPointAngle = 118
  HoleCutCountersinkAngle = 90
  HoleCutCustomValues = false
  HoleCutDepth = 0
  HoleCutDiameter = 0
  HoleCutType = 0
  ModelActualThread = false
  Profile = -> Sketch048
  Tapered = false
  TaperedAngle = 90
  ThreadAngle = 0
  ThreadClass = 0
  ThreadCutOffInner = 0
  ThreadCutOffOuter = 0
  ThreadDirection = 0
  ThreadFit = 0
  ThreadPitch = 0
  ThreadSize = 0
  ThreadType = 0
  Threaded = false
FEATURE [PartDesign::Hole] Hole030  label="ho-head-back-wheel-holes"
  BaseFeature = -> Hole029
  Depth = 25
  DepthType = 0
  Diameter = 5.3
  DrillForDepth = false
  DrillPoint = 1
  DrillPointAngle = 118
  HoleCutCountersinkAngle = 90
  HoleCutCustomValues = false
  HoleCutDepth = 0
  HoleCutDiameter = 6.1
  HoleCutType = 0
  ModelActualThread = false
  Profile = -> Sketch049
  Tapered = false
  TaperedAngle = 90
  ThreadAngle = 0
  ThreadClass = 0
  ThreadCutOffInner = 0
  ThreadCutOffOuter = 0
  ThreadDirection = 0
  ThreadFit = 1
  ThreadPitch = 0
  ThreadSize = 13
  ThreadType = 1
  Threaded = false
FEATURE [Sketcher::SketchObject] Sketch062  label="head-front-camera-fix-holes"
  ExternalGeometry = -> [Sketch056,Sketch057]
  FullyConstrained = false
  MapMode = 5
  Placement = pos=(0,0,6) rot=(0,0,1;0rad)
  Support = -> [Hole027]
  sketch-geometry (17):
    g0: Circle CenterX=-31 CenterY=-107 CenterZ=0 NormalX=0 NormalY=0 NormalZ=1 AngleXU=0 Radius=5.975
    g1: Circle CenterX=31 CenterY=-107 CenterZ=0 NormalX=0 NormalY=0 NormalZ=1 AngleXU=0 Radius=5.975
    g2: LineSegment StartX=-17.5 StartY=-48.1779 StartZ=0 EndX=-8.5 EndY=-48.1779 EndZ=0
    g3: LineSegment StartX=-8.5 StartY=-48.1779 StartZ=0 EndX=-8.5 EndY=-126.353 EndZ=0
    g4: LineSegment StartX=-8.5 StartY=-126.353 StartZ=0 EndX=-17.5 EndY=-126.353 EndZ=0
    g5: LineSegment StartX=-17.5 StartY=-126.353 StartZ=0 EndX=-17.5 EndY=-48.1779 EndZ=0
    g6: GeomPoint X=-13 Y=-126.353 Z=0
    g7: LineSegment StartX=8.5 StartY=-48.1779 StartZ=0 EndX=17.5 EndY=-48.1779 EndZ=0
    g8: LineSegment StartX=17.5 StartY=-48.1779 StartZ=0 EndX=17.5 EndY=-126.353 EndZ=0
    g9: LineSegment StartX=17.5 StartY=-126.353 StartZ=0 EndX=8.5 EndY=-126.353 EndZ=0
    g10: LineSegment StartX=8.5 StartY=-126.353 StartZ=0 EndX=8.5 EndY=-48.1779 EndZ=0
    g11: GeomPoint X=13 Y=-126.353 Z=0
    g12: GeomPoint X=-25.025 Y=-107 Z=0
    g13: GeomPoint X=-31 Y=-101.025 Z=0
    g14: LineSegment StartX=-31 StartY=-101.025 StartZ=0 EndX=31 EndY=-101.025 EndZ=0
    g15: Circle CenterX=-23.5 CenterY=-117 CenterZ=0 NormalX=0 NormalY=0 NormalZ=1 AngleXU=0 Radius=1.5
    g16: Circle CenterX=23.5 CenterY=-117 CenterZ=0 NormalX=0 NormalY=0 NormalZ=1 AngleXU=0 Radius=1.5
  constraints (41):
    c: Coincident(g0,g-3)
    c: Radius(g0) = 5.975
    c: Coincident(g1,g-4)
    c: Equal(g0,g1)
    c: Coincident(g2,g3)
    c: Coincident(g3,g4)
    c: Coincident(g4,g5)
    c: Coincident(g5,g2)
    c: Horizontal(g2)
    c: Horizontal(g4)
    c: Vertical(g3)
    c: Vertical(g5)
    c: Symmetric(g4,g4,g6)
    c: Vertical(g6,g-5)
    c: DistanceX(g2,g2) = 9
    c: Coincident(g7,g8)
    c: Coincident(g8,g9)
    c: Coincident(g9,g10)
    c: Coincident(g10,g7)
    c: Horizontal(g7)
    c: Horizontal(g9)
    c: Vertical(g8)
    c: Vertical(g10)
    c: Symmetric(g9,g9,g11)
    c: Vertical(g11,g-6)
    c: Horizontal(g3,g9)
    c: Equal(g2,g7)
    c: Equal(g3,g8)
    c: PointOnObject(g12,g0)
    c: Horizontal(g0,g12)
    c: PointOnObject(g13,g0)
    c: Vertical(g13,g0)
    c: Coincident(g14,g13)
    c: PointOnObject(g14,g1)
    c: Horizontal(g14)
    c: Equal(g15,g16)
    c: Equal(g16,g-5)
    c: Horizontal(g15,g16)
    c: DistanceX(g15,g4) = 6
    c: DistanceX(g8,g16) = 6
    c: DistanceY(g15,g12) = 10
FEATURE [PartDesign::Hole] Hole031  label="ho-head-front-camera-fix-holes"
  BaseFeature = -> Hole027
  Depth = 25
  DepthType = 0
  Diameter = 3.2
  DrillForDepth = false
  DrillPoint = 1
  DrillPointAngle = 118
  HoleCutCountersinkAngle = 90
  HoleCutCustomValues = false
  HoleCutDepth = 0
  HoleCutDiameter = 6.1
  HoleCutType = 0
  ModelActualThread = false
  Profile = -> Sketch062
  Tapered = false
  TaperedAngle = 90
  ThreadAngle = 0
  ThreadClass = 0
  ThreadCutOffInner = 0
  ThreadCutOffOuter = 0
  ThreadDirection = 0
  ThreadFit = 1
  ThreadPitch = 0
  ThreadSize = 9
  ThreadType = 1
  Threaded = false
FEATURE [Sketcher::SketchObject] Sketch063  label="head-back-camera-fix-holes"
  ExternalGeometry = -> [Binder]
  FullyConstrained = true
  MapMode = 5
  Placement = pos=(0,0,6) rot=(0,0,1;0rad)
  Support = -> [Hole030]
  sketch-geometry (2):
    g0: Circle CenterX=-23.5 CenterY=-117 CenterZ=0 NormalX=0 NormalY=0 NormalZ=1 AngleXU=0 Radius=1.6
    g1: Circle CenterX=23.5 CenterY=-117 CenterZ=0 NormalX=0 NormalY=0 NormalZ=1 AngleXU=0 Radius=1.6
  constraints (4):
    c: Equal(g0,g1)
    c: Equal(g1,g-3)
    c: Coincident(g0,g-3)
    c: Coincident(g1,g-4)
FEATURE [PartDesign::Hole] Hole032  label="ho-head-back-camera-fix-holes"
  BaseFeature = -> Hole030
  Depth = 25
  DepthType = 0
  Diameter = 2.5
  DrillForDepth = false
  DrillPoint = 1
  DrillPointAngle = 118
  HoleCutCountersinkAngle = 90
  HoleCutCustomValues = false
  HoleCutDepth = 0
  HoleCutDiameter = 6.1
  HoleCutType = 0
  ModelActualThread = false
  Profile = -> Sketch063
  Tapered = false
  TaperedAngle = 90
  ThreadAngle = 60
  ThreadClass = 0
  ThreadCutOffInner = 0.0541266
  ThreadCutOffOuter = 0.108253
  ThreadDirection = 0
  ThreadFit = 1
  ThreadPitch = 0.5
  ThreadSize = 9
  ThreadType = 1
  Threaded = true
